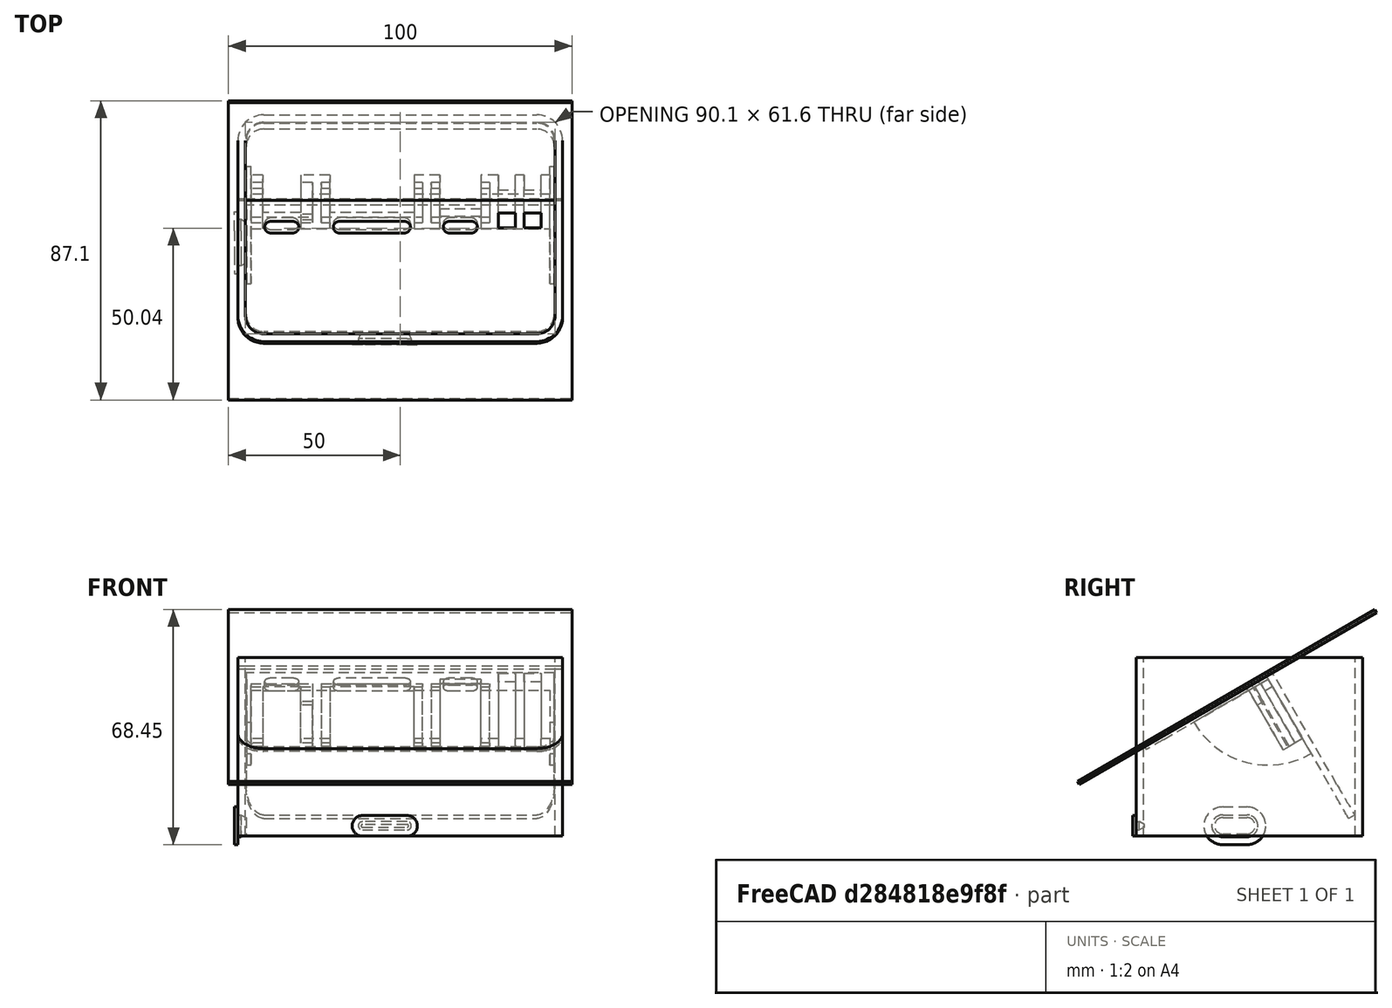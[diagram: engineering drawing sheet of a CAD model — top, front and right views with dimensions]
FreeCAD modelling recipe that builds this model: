
FCSTD DOCUMENT  (FreeCAD 0.21R33771 (Git))
Label: 2432S028_zz01
License: All rights reserved
LicenseURL: http://en.wikipedia.org/wiki/All_rights_reserved
objects: Part::Extrusion×22, Sketcher::SketchObject×21, Part::Box×9, Part::FeaturePython×8, Part::Cut×7, Part::Chamfer×6, Mesh::Feature×3, Part::MultiCommon×1, Part::MultiFuse×1
note: 75 computed .brp shape members not serialized (recipe doc carries the construction recipe); baked Part::Feature solids carry a one-line shape summary decoded from their .brp

FEATURE [Sketcher::SketchObject] Sketch  label="Basis"
  FullyConstrained = true
  sketch-geometry (22):
    g0: LineSegment StartX=-39.75 StartY=33 StartZ=0 EndX=39.75 EndY=33 EndZ=0
    g1: LineSegment StartX=47.25 StartY=25.5 StartZ=0 EndX=47.25 EndY=-25.5 EndZ=0
    g2: LineSegment StartX=39.75 StartY=-33 StartZ=0 EndX=-39.75 EndY=-33 EndZ=0
    g3: LineSegment StartX=-47.25 StartY=-25.5 StartZ=0 EndX=-47.25 EndY=25.5 EndZ=0
    g4: ArcOfCircle CenterX=-39.75 CenterY=25.5 CenterZ=0 NormalX=0 NormalY=0 NormalZ=1 AngleXU=0 Radius=7.5 StartAngle=1.5708 EndAngle=3.14159
    g5: GeomPoint X=-47.25 Y=33 Z=0
    g6: ArcOfCircle CenterX=39.75 CenterY=25.5 CenterZ=0 NormalX=0 NormalY=0 NormalZ=1 AngleXU=0 Radius=7.5 StartAngle=0 EndAngle=1.5708
    g7: GeomPoint X=47.25 Y=33 Z=0
    g8: ArcOfCircle CenterX=39.75 CenterY=-25.5 CenterZ=0 NormalX=0 NormalY=0 NormalZ=1 AngleXU=0 Radius=7.5 StartAngle=4.71239 EndAngle=6.28319
    g9: GeomPoint X=47.25 Y=-33 Z=0
    g10: ArcOfCircle CenterX=-39.75 CenterY=-25.5 CenterZ=0 NormalX=0 NormalY=0 NormalZ=1 AngleXU=0 Radius=7.5 StartAngle=3.14159 EndAngle=4.71239
    g11: GeomPoint X=-47.25 Y=-33 Z=0
    g12: ArcOfCircle CenterX=39.75 CenterY=17.9 CenterZ=0 NormalX=0 NormalY=0 NormalZ=1 AngleXU=0 Radius=5.5 StartAngle=4e-16 EndAngle=1.5708
    g13: LineSegment StartX=45.25 StartY=17.9 StartZ=0 EndX=45.25 EndY=-25.5 EndZ=0
    g14: ArcOfCircle CenterX=39.75 CenterY=-25.5 CenterZ=0 NormalX=0 NormalY=0 NormalZ=1 AngleXU=0 Radius=5.5 StartAngle=4.71239 EndAngle=6.28319
    g15: LineSegment StartX=39.75 StartY=-31 StartZ=0 EndX=-39.75 EndY=-31 EndZ=0
    g16: ArcOfCircle CenterX=-39.75 CenterY=-25.5 CenterZ=0 NormalX=0 NormalY=0 NormalZ=1 AngleXU=0 Radius=5.5 StartAngle=3.14159 EndAngle=4.71239
    g17: LineSegment StartX=-45.25 StartY=-25.5 StartZ=0 EndX=-45.25 EndY=17.9 EndZ=0
    g18: ArcOfCircle CenterX=-39.75 CenterY=17.9 CenterZ=0 NormalX=0 NormalY=0 NormalZ=1 AngleXU=0 Radius=5.5 StartAngle=1.5708 EndAngle=3.14159
    g19: LineSegment StartX=-39.75 StartY=23.4 StartZ=0 EndX=39.75 EndY=23.4 EndZ=0
    g20: GeomPoint X=45.25 Y=23.4 Z=0
    g21: GeomPoint X=-45.25 Y=-31 Z=0
  constraints (50):
    c: Horizontal(g0)
    c: Horizontal(g2)
    c: Vertical(g1)
    c: Vertical(g3)
    c: DistanceY(g9,g7) = 66
    c: Symmetric(g5,g9,g-1)
    c: PointOnObject(g5,g0)
    c: PointOnObject(g5,g3)
    c: Tangent(g0,g4) = 1.5708
    c: Tangent(g3,g4) = 1.5708
    c: PointOnObject(g7,g0)
    c: PointOnObject(g7,g1)
    c: Tangent(g0,g6) = 1.5708
    c: Tangent(g1,g6) = 1.5708
    c: PointOnObject(g9,g1)
    c: PointOnObject(g9,g2)
    c: Tangent(g1,g8) = 1.5708
    c: Tangent(g2,g8) = 1.5708
    c: PointOnObject(g11,g2)
    c: PointOnObject(g11,g3)
    c: Tangent(g2,g10) = 1.5708
    c: Tangent(g3,g10) = 1.5708
    c: Equal(g8,g10)
    c: Equal(g10,g4)
    c: Equal(g4,g6)
    c: Tangent(g12,g13) = 1.5708
    c: Tangent(g13,g14) = 1.5708
    c: Tangent(g14,g15) = 1.5708
    c: Tangent(g15,g16) = 1.5708
    c: Tangent(g16,g17) = 1.5708
    c: Tangent(g17,g18) = 1.5708
    c: Tangent(g18,g19) = 1.5708
    c: Tangent(g19,g12) = 1.5708
    c: Horizontal(g15)
    c: Vertical(g13)
    c: Vertical(g17)
    c: Equal(g12,g14)
    c: Equal(g14,g16)
    c: Equal(g16,g18)
    c: PointOnObject(g20,g13)
    c: PointOnObject(g20,g19)
    c: PointOnObject(g21,g15)
    c: PointOnObject(g21,g17)
    c: DistanceY(g14,g12) = 54.4
    c: DistanceX(g17,g12) = 90.5
    c: Diameter(g12) = 11
    c: Symmetric(g12,g17,g-2)
    c: DistanceY(g2,g14) = 2
    c: Coincident(g10,g16)
    c: DistanceY(g18,g4) = 2.1
FEATURE [Part::Box] Box  label="Cube"
  AttacherType = Attacher::AttachEngine3D
  Height = 100
  Length = 100
  Placement = pos=(-50,39.3072,-0.4) rot=(1,0,0;0.523599rad)
  Width = 100
FEATURE [Sketcher::SketchObject] Sketch001
  ExternalGeometry = -> [Sketch]
  FullyConstrained = true
  sketch-geometry (20):
    g0: ArcOfCircle CenterX=-39.75 CenterY=25.5 CenterZ=0 NormalX=0 NormalY=0 NormalZ=1 AngleXU=0 Radius=7.5 StartAngle=1.5708 EndAngle=3.14159
    g1: LineSegment StartX=-39.75 StartY=33 StartZ=0 EndX=39.75 EndY=33 EndZ=0
    g2: ArcOfCircle CenterX=39.75 CenterY=25.5 CenterZ=0 NormalX=0 NormalY=0 NormalZ=1 AngleXU=0 Radius=7.5 StartAngle=1e-16 EndAngle=1.5708
    g3: LineSegment StartX=47.25 StartY=25.5 StartZ=0 EndX=47.25 EndY=-25.5 EndZ=0
    g4: ArcOfCircle CenterX=39.75 CenterY=-25.5 CenterZ=0 NormalX=0 NormalY=0 NormalZ=1 AngleXU=0 Radius=7.5 StartAngle=4.71239 EndAngle=6.28319
    g5: LineSegment StartX=39.75 StartY=-33 StartZ=0 EndX=-39.75 EndY=-33 EndZ=0
    g6: ArcOfCircle CenterX=-39.75 CenterY=-25.5 CenterZ=0 NormalX=0 NormalY=0 NormalZ=1 AngleXU=0 Radius=7.5 StartAngle=3.14159 EndAngle=4.71239
    g7: LineSegment StartX=-47.25 StartY=-25.5 StartZ=0 EndX=-47.25 EndY=25.5 EndZ=0
    g8: GeomPoint X=-47.25 Y=33 Z=0
    g9: GeomPoint X=47.25 Y=-33 Z=0
    g10: ArcOfCircle CenterX=-39.75 CenterY=17.9 CenterZ=0 NormalX=0 NormalY=0 NormalZ=1 AngleXU=0 Radius=5.5 StartAngle=1.5708 EndAngle=3.14159
    g11: LineSegment StartX=-39.75 StartY=23.4 StartZ=0 EndX=39.75 EndY=23.4 EndZ=0
    g12: ArcOfCircle CenterX=39.75 CenterY=17.9 CenterZ=0 NormalX=0 NormalY=0 NormalZ=1 AngleXU=0 Radius=5.5 StartAngle=0 EndAngle=1.5708
    g13: LineSegment StartX=45.25 StartY=17.9 StartZ=0 EndX=45.25 EndY=-25.5 EndZ=0
    g14: ArcOfCircle CenterX=39.75 CenterY=-25.5 CenterZ=0 NormalX=0 NormalY=0 NormalZ=1 AngleXU=0 Radius=5.5 StartAngle=4.71239 EndAngle=6.28319
    g15: LineSegment StartX=39.75 StartY=-31 StartZ=0 EndX=-39.75 EndY=-31 EndZ=0
    g16: ArcOfCircle CenterX=-39.75 CenterY=-25.5 CenterZ=0 NormalX=0 NormalY=0 NormalZ=1 AngleXU=0 Radius=5.5 StartAngle=3.14159 EndAngle=4.71239
    g17: LineSegment StartX=-45.25 StartY=-25.5 StartZ=0 EndX=-45.25 EndY=17.9 EndZ=0
    g18: GeomPoint X=-45.25 Y=23.4 Z=0
    g19: GeomPoint X=45.25 Y=-31 Z=0
  constraints (44):
    c: Tangent(g0,g1) = 1.5708
    c: Tangent(g1,g2) = 1.5708
    c: Tangent(g2,g3) = 1.5708
    c: Tangent(g3,g4) = 1.5708
    c: Tangent(g4,g5) = 1.5708
    c: Tangent(g5,g6) = 1.5708
    c: Tangent(g6,g7) = 1.5708
    c: Tangent(g7,g0) = 1.5708
    c: Horizontal(g1)
    c: Horizontal(g5)
    c: Vertical(g3)
    c: Vertical(g7)
    c: Equal(g0,g2)
    c: Equal(g2,g4)
    c: Equal(g4,g6)
    c: PointOnObject(g8,g1)
    c: PointOnObject(g8,g7)
    c: PointOnObject(g9,g3)
    c: PointOnObject(g9,g5)
    c: Coincident(g-6,g4)
    c: Coincident(g0,g-3)
    c: Horizontal(g-3,g0)
    c: Tangent(g10,g11) = 1.5708
    c: Tangent(g11,g12) = 1.5708
    c: Tangent(g12,g13) = 1.5708
    c: Tangent(g13,g14) = 1.5708
    c: Tangent(g14,g15) = 1.5708
    c: Tangent(g15,g16) = 1.5708
    c: Tangent(g16,g17) = 1.5708
    c: Tangent(g17,g10) = 1.5708
    c: Horizontal(g11)
    c: Horizontal(g15)
    c: Vertical(g13)
    c: Vertical(g17)
    c: Equal(g10,g12)
    c: Equal(g12,g14)
    c: Equal(g14,g16)
    c: PointOnObject(g18,g11)
    c: PointOnObject(g18,g17)
    c: PointOnObject(g19,g13)
    c: PointOnObject(g19,g15)
    c: Coincident(g14,g4)
    c: Coincident(g10,g-5)
    c: Horizontal(g-5,g10)
FEATURE [Part::Extrusion] Extrude
  Base = -> Sketch001
  Dir = (0,0,1)
  DirMode = 2
  FaceMakerClass = Part::FaceMakerBullseye
  LengthFwd = 2
  LengthRev = 0
  Solid = true
  Symmetric = false
FEATURE [Sketcher::SketchObject] Sketch002
  ExternalGeometry = -> [Sketch]
  FullyConstrained = true
  Placement = pos=(0,0,2) rot=(0,0,1;0rad)
  sketch-geometry (26):
    g0: ArcOfCircle CenterX=-39.75 CenterY=25.5 CenterZ=0 NormalX=0 NormalY=0 NormalZ=1 AngleXU=0 Radius=7.5 StartAngle=1.5708 EndAngle=3.14159
    g1: LineSegment StartX=-39.75 StartY=33 StartZ=0 EndX=39.75 EndY=33 EndZ=0
    g2: ArcOfCircle CenterX=39.75 CenterY=25.5 CenterZ=0 NormalX=0 NormalY=0 NormalZ=1 AngleXU=0 Radius=7.5 StartAngle=4e-16 EndAngle=1.5708
    g3: LineSegment StartX=47.25 StartY=25.5 StartZ=0 EndX=47.25 EndY=-25.5 EndZ=0
    g4: ArcOfCircle CenterX=39.75 CenterY=-25.5 CenterZ=0 NormalX=0 NormalY=0 NormalZ=1 AngleXU=0 Radius=7.5 StartAngle=4.71239 EndAngle=6.28319
    g5: LineSegment StartX=39.75 StartY=-33 StartZ=0 EndX=-39.75 EndY=-33 EndZ=0
    g6: ArcOfCircle CenterX=-39.75 CenterY=-25.5 CenterZ=0 NormalX=0 NormalY=0 NormalZ=1 AngleXU=0 Radius=7.5 StartAngle=3.14159 EndAngle=4.71239
    g7: LineSegment StartX=-47.25 StartY=-25.5 StartZ=0 EndX=-47.25 EndY=25.5 EndZ=0
    g8: GeomPoint X=-47.25 Y=33 Z=0
    g9: GeomPoint X=47.25 Y=-33 Z=0
    g10: ArcOfCircle CenterX=-39.75 CenterY=17.9 CenterZ=0 NormalX=0 NormalY=0 NormalZ=1 AngleXU=0 Radius=5.5 StartAngle=1.5708 EndAngle=3.14159
    g11: LineSegment StartX=-39.75 StartY=23.4 StartZ=0 EndX=39.75 EndY=23.4 EndZ=0
    g12: ArcOfCircle CenterX=39.75 CenterY=17.9 CenterZ=0 NormalX=0 NormalY=0 NormalZ=1 AngleXU=0 Radius=5.5 StartAngle=0 EndAngle=1.5708
    g13: LineSegment StartX=45.25 StartY=17.9 StartZ=0 EndX=45.25 EndY=-25.5 EndZ=0
    g14: ArcOfCircle CenterX=39.75 CenterY=-25.5 CenterZ=0 NormalX=0 NormalY=0 NormalZ=1 AngleXU=0 Radius=5.5 StartAngle=4.71239 EndAngle=6.28319
    g15: LineSegment StartX=39.75 StartY=-31 StartZ=0 EndX=-39.75 EndY=-31 EndZ=0
    g16: ArcOfCircle CenterX=-39.75 CenterY=-25.5 CenterZ=0 NormalX=0 NormalY=0 NormalZ=1 AngleXU=0 Radius=5.5 StartAngle=3.14159 EndAngle=4.71239
    g17: LineSegment StartX=-45.25 StartY=-25.5 StartZ=0 EndX=-45.25 EndY=17.9 EndZ=0
    g18: GeomPoint X=-45.25 Y=23.4 Z=0
    g19: GeomPoint X=45.25 Y=-31 Z=0
    g20: ArcOfCircle CenterX=-39.75 CenterY=25.5 CenterZ=0 NormalX=0 NormalY=0 NormalZ=1 AngleXU=0 Radius=5.5 StartAngle=1.5708 EndAngle=3.14159
    g21: LineSegment StartX=-39.75 StartY=31 StartZ=0 EndX=39.75 EndY=31 EndZ=0
    g22: ArcOfCircle CenterX=39.75 CenterY=25.5 CenterZ=0 NormalX=0 NormalY=0 NormalZ=1 AngleXU=0 Radius=5.5 StartAngle=0 EndAngle=1.5708
    g23: LineSegment StartX=-45.25 StartY=25.4 StartZ=0 EndX=45.25 EndY=25.4 EndZ=0
    g24: LineSegment StartX=-45.25 StartY=25.5 StartZ=0 EndX=-45.25 EndY=25.4 EndZ=0
    g25: LineSegment StartX=45.25 StartY=25.5 StartZ=0 EndX=45.25 EndY=25.4 EndZ=0
  constraints (62):
    c: Tangent(g0,g1) = 1.5708
    c: Tangent(g1,g2) = 1.5708
    c: Tangent(g2,g3) = 1.5708
    c: Tangent(g3,g4) = 1.5708
    c: Tangent(g4,g5) = 1.5708
    c: Tangent(g5,g6) = 1.5708
    c: Tangent(g6,g7) = 1.5708
    c: Tangent(g7,g0) = 1.5708
    c: Horizontal(g1)
    c: Horizontal(g5)
    c: Vertical(g3)
    c: Vertical(g7)
    c: Equal(g0,g2)
    c: Equal(g2,g4)
    c: Equal(g4,g6)
    c: PointOnObject(g8,g1)
    c: PointOnObject(g8,g7)
    c: PointOnObject(g9,g3)
    c: PointOnObject(g9,g5)
    c: Coincident(g4,g-6)
    c: Coincident(g0,g-3)
    c: Horizontal(g-3,g0)
    c: Tangent(g10,g11) = 1.5708
    c: Tangent(g11,g12) = 1.5708
    c: Tangent(g12,g13) = 1.5708
    c: Tangent(g13,g14) = 1.5708
    c: Tangent(g14,g15) = 1.5708
    c: Tangent(g15,g16) = 1.5708
    c: Tangent(g16,g17) = 1.5708
    c: Tangent(g17,g10) = 1.5708
    c: Horizontal(g11)
    c: Horizontal(g15)
    c: Vertical(g13)
    c: Vertical(g17)
    c: Equal(g10,g12)
    c: Equal(g12,g14)
    c: Equal(g14,g16)
    c: PointOnObject(g18,g11)
    c: PointOnObject(g18,g17)
    c: PointOnObject(g19,g13)
    c: PointOnObject(g19,g15)
    c: Coincident(g4,g14)
    c: Coincident(g10,g-5)
    c: Horizontal(g14,g-6)
    c: Coincident(g20,g0)
    c: Vertical(g0,g20)
    c: Horizontal(g0,g20)
    c: DistanceY(g20,g0) = 2
    c: Coincident(g21,g20)
    c: Horizontal(g21)
    c: Coincident(g22,g2)
    c: Coincident(g22,g21)
    c: Equal(g22,g20)
    c: Horizontal(g2,g22)
    c: Horizontal(g23)
    c: Coincident(g24,g20)
    c: Coincident(g24,g23)
    c: Vertical(g24)
    c: Coincident(g25,g22)
    c: Coincident(g25,g23)
    c: Vertical(g25)
    c: DistanceY(g10,g23) = 2
FEATURE [Part::Extrusion] Extrude001  label="Extrude_2mm"
  Base = -> Sketch002
  Dir = (0,0,1)
  DirMode = 2
  FaceMakerClass = Part::FaceMakerBullseye
  LengthFwd = 2
  LengthRev = 0
  Solid = true
  Symmetric = false
FEATURE [Sketcher::SketchObject] Sketch003
  ExternalGeometry = -> [Sketch]
  FullyConstrained = true
  Placement = pos=(0,0,4) rot=(0,0,1;0rad)
  sketch-geometry (20):
    g0: ArcOfCircle CenterX=-39.75 CenterY=25.5 CenterZ=0 NormalX=0 NormalY=0 NormalZ=1 AngleXU=0 Radius=7.5 StartAngle=1.5708 EndAngle=3.14159
    g1: LineSegment StartX=-39.75 StartY=33 StartZ=0 EndX=39.75 EndY=33 EndZ=0
    g2: ArcOfCircle CenterX=39.75 CenterY=25.5 CenterZ=0 NormalX=0 NormalY=0 NormalZ=1 AngleXU=0 Radius=7.5 StartAngle=0 EndAngle=1.5708
    g3: LineSegment StartX=47.25 StartY=25.5 StartZ=0 EndX=47.25 EndY=-25.5 EndZ=0
    g4: ArcOfCircle CenterX=39.75 CenterY=-25.5 CenterZ=0 NormalX=0 NormalY=0 NormalZ=1 AngleXU=0 Radius=7.5 StartAngle=4.71239 EndAngle=6.28319
    g5: LineSegment StartX=39.75 StartY=-33 StartZ=0 EndX=-39.75 EndY=-33 EndZ=0
    g6: ArcOfCircle CenterX=-39.75 CenterY=-25.5 CenterZ=0 NormalX=0 NormalY=0 NormalZ=1 AngleXU=0 Radius=7.5 StartAngle=3.14159 EndAngle=4.71239
    g7: LineSegment StartX=-47.25 StartY=-25.5 StartZ=0 EndX=-47.25 EndY=25.5 EndZ=0
    g8: GeomPoint X=-47.25 Y=33 Z=0
    g9: GeomPoint X=47.25 Y=-33 Z=0
    g10: ArcOfCircle CenterX=-39.75 CenterY=25.5 CenterZ=0 NormalX=0 NormalY=0 NormalZ=1 AngleXU=0 Radius=5.5 StartAngle=1.5708 EndAngle=3.14159
    g11: LineSegment StartX=-39.75 StartY=31 StartZ=0 EndX=39.75 EndY=31 EndZ=0
    g12: ArcOfCircle CenterX=39.75 CenterY=25.5 CenterZ=0 NormalX=0 NormalY=0 NormalZ=1 AngleXU=0 Radius=5.5 StartAngle=0 EndAngle=1.5708
    g13: LineSegment StartX=45.25 StartY=25.5 StartZ=0 EndX=45.25 EndY=-25.5 EndZ=0
    g14: ArcOfCircle CenterX=39.75 CenterY=-25.5 CenterZ=0 NormalX=0 NormalY=0 NormalZ=1 AngleXU=0 Radius=5.5 StartAngle=4.71239 EndAngle=6.28319
    g15: LineSegment StartX=39.75 StartY=-31 StartZ=0 EndX=-39.75 EndY=-31 EndZ=0
    g16: ArcOfCircle CenterX=-39.75 CenterY=-25.5 CenterZ=0 NormalX=0 NormalY=0 NormalZ=1 AngleXU=0 Radius=5.5 StartAngle=3.14159 EndAngle=4.71239
    g17: LineSegment StartX=-45.25 StartY=-25.5 StartZ=0 EndX=-45.25 EndY=25.5 EndZ=0
    g18: GeomPoint X=-45.25 Y=31 Z=0
    g19: GeomPoint X=45.25 Y=-31 Z=0
  constraints (45):
    c: Tangent(g0,g1) = 1.5708
    c: Tangent(g1,g2) = 1.5708
    c: Tangent(g2,g3) = 1.5708
    c: Tangent(g3,g4) = 1.5708
    c: Tangent(g4,g5) = 1.5708
    c: Tangent(g5,g6) = 1.5708
    c: Tangent(g6,g7) = 1.5708
    c: Tangent(g7,g0) = 1.5708
    c: Horizontal(g1)
    c: Horizontal(g5)
    c: Vertical(g3)
    c: Vertical(g7)
    c: Equal(g0,g2)
    c: Equal(g2,g4)
    c: Equal(g4,g6)
    c: PointOnObject(g8,g1)
    c: PointOnObject(g8,g7)
    c: PointOnObject(g9,g3)
    c: PointOnObject(g9,g5)
    c: Coincident(g-5,g4)
    c: Coincident(g0,g-3)
    c: Horizontal(g-3,g0)
    c: Tangent(g10,g11) = 1.5708
    c: Tangent(g12,g13) = 1.5708
    c: Tangent(g13,g14) = 1.5708
    c: Tangent(g14,g15) = 1.5708
    c: Tangent(g15,g16) = 1.5708
    c: Tangent(g16,g17) = 1.5708
    c: Tangent(g17,g10) = 1.5708
    c: Horizontal(g11)
    c: Horizontal(g15)
    c: Vertical(g13)
    c: Vertical(g17)
    c: Equal(g10,g12)
    c: Equal(g12,g14)
    c: Equal(g14,g16)
    c: PointOnObject(g18,g11)
    c: PointOnObject(g18,g17)
    c: PointOnObject(g19,g13)
    c: PointOnObject(g19,g15)
    c: Coincident(g14,g4)
    c: Coincident(g11,g12)
    c: Coincident(g0,g10)
    c: Horizontal(g15,g-6)
    c: Vertical(g12,g11)
FEATURE [Part::Extrusion] Extrude002  label="Extrude_4mm"
  Base = -> Sketch003
  Dir = (0,0,1)
  DirMode = 2
  FaceMakerClass = Part::FaceMakerBullseye
  LengthFwd = 10
  LengthRev = 0
  Solid = true
  Symmetric = false
FEATURE [Part::Extrusion] Extrude003  label="Extrude_6mm"
  Base = -> Sketch003
  Dir = (0,0,1)
  DirMode = 2
  FaceMakerClass = Part::FaceMakerBullseye
  LengthFwd = 52
  LengthRev = 0
  Solid = true
  Symmetric = false
FEATURE [Part::Box] Box001  label="Cube001"
  AttacherType = Attacher::AttachEngine3D
  Height = 100
  Length = 100
  Placement = pos=(-50,-49.5397,19.0874) rot=(1,0,0;0.523599rad)
  Width = 100
FEATURE [Part::Box] Box002  label="Cube002"
  AttacherType = Attacher::AttachEngine3D
  Height = 100
  Length = 100
  Placement = pos=(-50,37.5751,-1.4) rot=(1,0,0;0.523599rad)
  Width = 2
FEATURE [Sketcher::SketchObject] Sketch004
  ExternalGeometry = -> [Sketch]
  FullyConstrained = false
  sketch-geometry (12):
    g0: ArcOfCircle CenterX=-39.75 CenterY=25.5 CenterZ=0 NormalX=0 NormalY=0 NormalZ=1 AngleXU=0 Radius=7.5 StartAngle=1.5708 EndAngle=3.14159
    g1: LineSegment StartX=-39.75 StartY=33 StartZ=0 EndX=39.75 EndY=33 EndZ=0
    g2: ArcOfCircle CenterX=39.75 CenterY=25.5 CenterZ=0 NormalX=0 NormalY=0 NormalZ=1 AngleXU=0 Radius=7.5 StartAngle=1e-16 EndAngle=1.5708
    g3: LineSegment StartX=47.25 StartY=25.5 StartZ=0 EndX=47.25 EndY=-25.5 EndZ=0
    g4: ArcOfCircle CenterX=39.75 CenterY=-25.5 CenterZ=0 NormalX=0 NormalY=0 NormalZ=1 AngleXU=0 Radius=7.5 StartAngle=4.71239 EndAngle=6.28319
    g5: LineSegment StartX=39.75 StartY=-33 StartZ=0 EndX=-39.75 EndY=-33 EndZ=0
    g6: ArcOfCircle CenterX=-39.75 CenterY=-25.5 CenterZ=0 NormalX=0 NormalY=0 NormalZ=1 AngleXU=0 Radius=7.5 StartAngle=3.14159 EndAngle=4.71239
    g7: LineSegment StartX=-47.25 StartY=-25.5 StartZ=0 EndX=-47.25 EndY=25.5 EndZ=0
    g8: GeomPoint X=-47.25 Y=33 Z=0
    g9: GeomPoint X=47.25 Y=-33 Z=0
    g10: GeomPoint X=-22 Y=14 Z=0
    g11: GeomPoint X=22 Y=-30 Z=0
  constraints (22):
    c: Tangent(g0,g1) = 1.5708
    c: Tangent(g1,g2) = 1.5708
    c: Tangent(g2,g3) = 1.5708
    c: Tangent(g3,g4) = 1.5708
    c: Tangent(g4,g5) = 1.5708
    c: Tangent(g5,g6) = 1.5708
    c: Tangent(g6,g7) = 1.5708
    c: Tangent(g7,g0) = 1.5708
    c: Horizontal(g1)
    c: Horizontal(g5)
    c: Vertical(g3)
    c: Vertical(g7)
    c: Equal(g0,g2)
    c: Equal(g2,g4)
    c: Equal(g4,g6)
    c: PointOnObject(g8,g1)
    c: PointOnObject(g8,g7)
    c: PointOnObject(g9,g3)
    c: PointOnObject(g9,g5)
    c: Coincident(g0,g-3)
    c: Horizontal(g-3,g0)
    c: Coincident(g4,g-4)
FEATURE [Part::Extrusion] Extrude004
  Base = -> Sketch004
  Dir = (0,0,1)
  DirMode = 2
  FaceMakerClass = Part::FaceMakerBullseye
  LengthFwd = 56
  LengthRev = 0
  Solid = true
  Symmetric = false
FEATURE [Part::MultiCommon] Common
  Shapes = -> [Box002,Extrude004]
FEATURE [Part::MultiFuse] Fusion
  Shapes = -> [Common,Extrude,Extrude001,Extrude002,Extrude003]
FEATURE [Part::Cut] Cut
  Base = -> Fusion
  Tool = -> Box
FEATURE [Part::Cut] Cut001
  Base = -> Cut
  Tool = -> Box001
FEATURE [Part::Box] Box003  label="Cube003"
  AttacherType = Attacher::AttachEngine3D
  Height = 3
  Length = 1.5
  Placement = pos=(43.75,-29,7) rot=(0,0,1;0rad)
  Width = 14.7
FEATURE [Part::Chamfer] Chamfer
  Base = -> Box003
  Edges = 4 edges r=1.49: [Edge1,Edge2,Edge3,Edge4]
FEATURE [Part::Box] Box004  label="Cube004"
  AttacherType = Attacher::AttachEngine3D
  Height = 3
  Length = 1.5
  Placement = pos=(-45.25,-29,8) rot=(0,0,1;0rad)
  Width = 14.7
FEATURE [Part::Chamfer] Chamfer001
  Base = -> Box004
  Edges = 4 edges r=1.49: [Edge5,Edge6,Edge7,Edge8]
FEATURE [Sketcher::SketchObject] Sketch005  label="Basis001_bEZEL"
  FullyConstrained = true
  Placement = pos=(0,-2.75,0) rot=(0,1,0;3.14159rad)
  sketch-geometry (46):
    g0: ArcOfCircle CenterX=40 CenterY=22 CenterZ=0 NormalX=0 NormalY=0 NormalZ=1 AngleXU=0 Radius=3 StartAngle=4e-16 EndAngle=1.5708
    g1: LineSegment StartX=43 StartY=22 StartZ=0 EndX=43 EndY=-22 EndZ=0
    g2: ArcOfCircle CenterX=40 CenterY=-22 CenterZ=0 NormalX=0 NormalY=0 NormalZ=1 AngleXU=0 Radius=3 StartAngle=4.71239 EndAngle=6.28319
    g3: LineSegment StartX=40 StartY=-25 StartZ=0 EndX=-40 EndY=-25 EndZ=0
    g4: ArcOfCircle CenterX=-40 CenterY=-22 CenterZ=0 NormalX=0 NormalY=0 NormalZ=1 AngleXU=0 Radius=3 StartAngle=3.14159 EndAngle=4.71239
    g5: LineSegment StartX=-43 StartY=-22 StartZ=0 EndX=-43 EndY=22 EndZ=0
    g6: ArcOfCircle CenterX=-40 CenterY=22 CenterZ=0 NormalX=0 NormalY=0 NormalZ=1 AngleXU=0 Radius=3 StartAngle=1.5708 EndAngle=3.14159
    g7: LineSegment StartX=-40 StartY=25 StartZ=0 EndX=40 EndY=25 EndZ=0
    g8: GeomPoint X=43 Y=25 Z=0
    g9: GeomPoint X=-43 Y=-25 Z=0
    g10: Circle CenterX=-39 CenterY=21 CenterZ=0 NormalX=0 NormalY=0 NormalZ=1 AngleXU=0 Radius=1.6
    g11: Circle CenterX=-39 CenterY=-21 CenterZ=0 NormalX=0 NormalY=0 NormalZ=1 AngleXU=0 Radius=1.6
    g12: Circle CenterX=39 CenterY=21 CenterZ=0 NormalX=0 NormalY=0 NormalZ=1 AngleXU=0 Radius=1.6
    g13: Circle CenterX=39 CenterY=-21 CenterZ=0 NormalX=0 NormalY=0 NormalZ=1 AngleXU=0 Radius=1.6
    g14: LineSegment StartX=-35 StartY=25 StartZ=0 EndX=36 EndY=25 EndZ=0
    g15: LineSegment StartX=36 StartY=25 StartZ=0 EndX=36 EndY=-25 EndZ=0
    g16: LineSegment StartX=36 StartY=-25 StartZ=0 EndX=-35 EndY=-25 EndZ=0
    g17: LineSegment StartX=-35 StartY=-25 StartZ=0 EndX=-35 EndY=25 EndZ=0
    g18: LineSegment StartX=-40.4 StartY=-12 StartZ=0 EndX=-37.4 EndY=-12 EndZ=0
    g19: LineSegment StartX=-37.4 StartY=-12 StartZ=0 EndX=-37.4 EndY=-17 EndZ=0
    g20: LineSegment StartX=-37.4 StartY=-17 StartZ=0 EndX=-40.4 EndY=-17 EndZ=0
    g21: LineSegment StartX=-40.4 StartY=-17 StartZ=0 EndX=-40.4 EndY=-12 EndZ=0
    g22: LineSegment StartX=-2 StartY=-25 StartZ=0 EndX=11 EndY=-25 EndZ=0
    g23: LineSegment StartX=11 StartY=-25 StartZ=0 EndX=11 EndY=-28 EndZ=0
    g24: LineSegment StartX=11 StartY=-28 StartZ=0 EndX=-2 EndY=-28 EndZ=0
    g25: LineSegment StartX=-2 StartY=-28 StartZ=0 EndX=-2 EndY=-25 EndZ=0
    g26: LineSegment StartX=43 StartY=3 StartZ=0 EndX=53 EndY=3 EndZ=0
    g27: LineSegment StartX=53 StartY=3 StartZ=0 EndX=53 EndY=-6 EndZ=0
    g28: LineSegment StartX=53 StartY=-6 StartZ=0 EndX=43 EndY=-6 EndZ=0
    g29: LineSegment StartX=43 StartY=-6 StartZ=0 EndX=43 EndY=3 EndZ=0
    g30: LineSegment StartX=43 StartY=14 StartZ=0 EndX=45 EndY=14 EndZ=0
    g31: LineSegment StartX=45 StartY=14 StartZ=0 EndX=45 EndY=6 EndZ=0
    g32: LineSegment StartX=45 StartY=6 StartZ=0 EndX=43 EndY=6 EndZ=0
    g33: LineSegment StartX=43 StartY=6 StartZ=0 EndX=43 EndY=14 EndZ=0
    g34: LineSegment StartX=-31.5 StartY=-25 StartZ=0 EndX=-23.5 EndY=-25 EndZ=0
    g35: LineSegment StartX=-23.5 StartY=-25 StartZ=0 EndX=-23.5 EndY=-27 EndZ=0
    g36: LineSegment StartX=-23.5 StartY=-27 StartZ=0 EndX=-31.5 EndY=-27 EndZ=0
    g37: LineSegment StartX=-31.5 StartY=-27 StartZ=0 EndX=-31.5 EndY=-25 EndZ=0
    g38: LineSegment StartX=-16.5 StartY=-25 StartZ=0 EndX=-8.5 EndY=-25 EndZ=0
    g39: LineSegment StartX=-8.5 StartY=-25 StartZ=0 EndX=-8.5 EndY=-27 EndZ=0
    g40: LineSegment StartX=-8.5 StartY=-27 StartZ=0 EndX=-16.5 EndY=-27 EndZ=0
    g41: LineSegment StartX=-16.5 StartY=-27 StartZ=0 EndX=-16.5 EndY=-25 EndZ=0
    g42: LineSegment StartX=-33 StartY=22.5 StartZ=0 EndX=27 EndY=22.5 EndZ=0
    g43: LineSegment StartX=27 StartY=22.5 StartZ=0 EndX=27 EndY=-22.5 EndZ=0
    g44: LineSegment StartX=27 StartY=-22.5 StartZ=0 EndX=-33 EndY=-22.5 EndZ=0
    g45: LineSegment StartX=-33 StartY=-22.5 StartZ=0 EndX=-33 EndY=22.5 EndZ=0
  constraints (130):
    c: Tangent(g0,g1) = 1.5708
    c: Tangent(g1,g2) = 1.5708
    c: Tangent(g2,g3) = 1.5708
    c: Tangent(g3,g4) = 1.5708
    c: Tangent(g4,g5) = 1.5708
    c: Tangent(g5,g6) = 1.5708
    c: Tangent(g6,g7) = 1.5708
    c: Tangent(g7,g0) = 1.5708
    c: Horizontal(g3)
    c: Vertical(g1)
    c: Vertical(g5)
    c: Equal(g0,g2)
    c: Equal(g2,g4)
    c: Equal(g4,g6)
    c: PointOnObject(g8,g1)
    c: PointOnObject(g8,g7)
    c: PointOnObject(g9,g3)
    c: PointOnObject(g9,g5)
    c: DistanceY(g2,g0) = 50
    c: DistanceX(g5,g0) = 86
    c: Diameter(g0) = 6
    c: Symmetric(g6,g2,g-1)
    c: Horizontal(g7)
    c: Diameter(g10) = 3.2
    c: DistanceY(g10,g6) = 4
    c: DistanceX(g5,g10) = 4
    c: Equal(g10,g12)
    c: Horizontal(g10,g12)
    c: Vertical(g10,g11)
    c: Horizontal(g11,g13)
    c: Vertical(g13,g12)
    c: Equal(g10,g11)
    c: Equal(g11,g13)
    c: DistanceY(g2,g13) = 4
    c: DistanceX(g13,g1) = 4
    c: Coincident(g14,g15)
    c: Coincident(g15,g16)
    c: Coincident(g16,g17)
    c: Coincident(g17,g14)
    c: Horizontal(g14)
    c: Horizontal(g16)
    c: Vertical(g15)
    c: Vertical(g17)
    c: PointOnObject(g14,g7)
    c: PointOnObject(g16,g3)
    c: DistanceX(g14,g0) = 7
    c: DistanceX(g5,g14) = 8
    c: Coincident(g18,g19)
    c: Coincident(g19,g20)
    c: Coincident(g20,g21)
    c: Coincident(g21,g18)
    c: Horizontal(g18)
    c: Horizontal(g20)
    c: Vertical(g19)
    c: Vertical(g21)
    c: DistanceX(g20,g20) = 3
    c: DistanceY(g21,g21) = 5
    c: DistanceY(g3,g20) = 8
    c: DistanceX(g4,g20) = 2.6
    c: Coincident(g22,g23)
    c: Coincident(g23,g24)
    c: Coincident(g24,g25)
    c: Coincident(g25,g22)
    c: Horizontal(g22)
    c: Horizontal(g24)
    c: Vertical(g23)
    c: Vertical(g25)
    c: PointOnObject(g22,g3)
    c: DistanceX(g4,g22) = 41
    c: DistanceX(g22,g1) = 32
    c: DistanceY(g23,g23) = 3
    c: Coincident(g26,g27)
    c: Coincident(g27,g28)
    c: Coincident(g28,g29)
    c: Coincident(g29,g26)
    c: Horizontal(g26)
    c: Horizontal(g28)
    c: Vertical(g27)
    c: Vertical(g29)
    c: PointOnObject(g26,g1)
    c: DistanceY(g26,g0) = 22
    c: DistanceY(g2,g28) = 19
    c: DistanceX(g26,g26) = 10
    c: Coincident(g30,g31)
    c: Coincident(g31,g32)
    c: Coincident(g32,g33)
    c: Coincident(g33,g30)
    c: Horizontal(g30)
    c: Horizontal(g32)
    c: Vertical(g31)
    c: Vertical(g33)
    c: PointOnObject(g30,g1)
    c: DistanceY(g30,g0) = 11
    c: DistanceY(g2,g32) = 31
    c: DistanceX(g30,g30) = 2
    c: Coincident(g34,g35)
    c: Coincident(g35,g36)
    c: Coincident(g36,g37)
    c: Coincident(g37,g34)
    c: Horizontal(g34)
    c: Horizontal(g36)
    c: Vertical(g35)
    c: Vertical(g37)
    c: PointOnObject(g34,g3)
    c: Coincident(g38,g39)
    c: Coincident(g39,g40)
    c: Coincident(g40,g41)
    c: Coincident(g41,g38)
    c: Horizontal(g38)
    c: Horizontal(g40)
    c: Vertical(g39)
    c: Vertical(g41)
    c: PointOnObject(g38,g3)
    c: Equal(g31,g40)
    c: Equal(g40,g36)
    c: Equal(g32,g39)
    c: Equal(g39,g35)
    c: DistanceX(g4,g34) = 11.5
    c: DistanceX(g4,g38) = 26.5
    c: Coincident(g42,g43)
    c: Coincident(g43,g44)
    c: Coincident(g44,g45)
    c: Coincident(g45,g42)
    c: Horizontal(g42)
    c: Horizontal(g44)
    c: Vertical(g43)
    c: DistanceX(g44,g44) = 60
    c: DistanceY(g43,g43) = 45
    c: Symmetric(g42,g44,g-1)
    c: DistanceX(g14,g42) = 2
FEATURE [Sketcher::SketchObject] Sketch006
  ExternalGeometry = -> [Sketch005]
  FullyConstrained = true
  MapMode = 5
  Placement = pos=(0,-33,0) rot=(1,0,0;1.5708rad)
  Support = -> [Cut001]
  sketch-geometry (4):
    g0: ArcOfCircle CenterX=2 CenterY=7 CenterZ=0 NormalX=0 NormalY=0 NormalZ=1 AngleXU=0 Radius=1.5 StartAngle=4.71239 EndAngle=7.85398
    g1: ArcOfCircle CenterX=-11 CenterY=7 CenterZ=0 NormalX=0 NormalY=0 NormalZ=1 AngleXU=0 Radius=1.5 StartAngle=1.5708 EndAngle=4.71239
    g2: LineSegment StartX=2 StartY=8.5 StartZ=0 EndX=-11 EndY=8.5 EndZ=0
    g3: LineSegment StartX=-11 StartY=5.5 StartZ=0 EndX=2 EndY=5.5 EndZ=0
  constraints (10):
    c: Tangent(g0,g2) = -1.5708
    c: Tangent(g2,g1) = -1.5708
    c: Tangent(g1,g3) = -1.5708
    c: Tangent(g3,g0) = -1.5708
    c: Equal(g0,g1)
    c: Horizontal(g2)
    c: DistanceY(g-1,g1) = 7
    c: Diameter(g1) = 3
    c: Vertical(g1,g-3)
    c: Vertical(g0,g-3)
FEATURE [Part::Extrusion] Extrude005
  Base = -> Sketch006
  Dir = (0,-1,2e-16)
  DirMode = 2
  FaceMakerClass = Part::FaceMakerBullseye
  LengthFwd = 3
  LengthRev = 0
  Reversed = true
  Solid = true
  Symmetric = false
FEATURE [Sketcher::SketchObject] Sketch007
  ExternalGeometry = -> [Sketch005]
  FullyConstrained = true
  MapMode = 5
  Placement = pos=(-47.25,0,0) rot=(0.57735,-0.57735,-0.57735;2.0944rad)
  Support = -> [Cut001]
  sketch-geometry (6):
    g0: ArcOfCircle CenterX=0.75 CenterY=7 CenterZ=0 NormalX=0 NormalY=0 NormalZ=1 AngleXU=0 Radius=3.5 StartAngle=1.5708 EndAngle=4.71239
    g1: ArcOfCircle CenterX=7.75 CenterY=7 CenterZ=0 NormalX=0 NormalY=0 NormalZ=1 AngleXU=0 Radius=3.5 StartAngle=4.71239 EndAngle=7.85398
    g2: LineSegment StartX=0.75 StartY=3.5 StartZ=0 EndX=7.75 EndY=3.5 EndZ=0
    g3: LineSegment StartX=7.75 StartY=10.5 StartZ=0 EndX=0.75 EndY=10.5 EndZ=0
    g4: LineSegment StartX=-0.25 StartY=-6.5e-15 StartZ=0 EndX=0.75 EndY=3.5 EndZ=0
    g5: LineSegment StartX=7.75 StartY=3.5 StartZ=0 EndX=8.75 EndY=-6.7e-15 EndZ=0
  constraints (14):
    c: Tangent(g0,g2) = -1.5708
    c: Tangent(g2,g1) = -1.5708
    c: Tangent(g1,g3) = -1.5708
    c: Tangent(g3,g0) = -1.5708
    c: Equal(g0,g1)
    c: Horizontal(g2)
    c: DistanceY(g-1,g1) = 7
    c: Diameter(g1) = 7
    c: DistanceX(g3,g3) = 7
    c: Coincident(g4,g-3)
    c: Coincident(g4,g0)
    c: Coincident(g5,g1)
    c: Coincident(g5,g-3)
    c: Equal(g5,g4)
FEATURE [Part::Extrusion] Extrude006
  Base = -> Sketch007
  Dir = (-1,0,0)
  DirMode = 2
  FaceMakerClass = Part::FaceMakerBullseye
  LengthFwd = 3
  LengthRev = 0
  Reversed = true
  Solid = true
  Symmetric = false
FEATURE [Part::Box] Box005  label="Cube005"
  AttacherType = Attacher::AttachEngine3D
  Height = 3
  Length = 1.5
  Placement = pos=(43.75,10,7) rot=(0,0,1;0rad)
  Width = 14.7
FEATURE [Part::Chamfer] Chamfer002
  Base = -> Box005
  Edges = 4 edges r=1.49: [Edge1,Edge2,Edge3,Edge4]
FEATURE [Part::Box] Box006  label="Cube006"
  AttacherType = Attacher::AttachEngine3D
  Height = 3
  Length = 1.5
  Placement = pos=(-45.25,10,8) rot=(0,0,1;0rad)
  Width = 14.7
FEATURE [Part::Chamfer] Chamfer003
  Base = -> Box006
  Edges = 4 edges r=1.49: [Edge5,Edge6,Edge7,Edge8]
FEATURE [Part::Cut] Cut002
  Base = -> Cut001
  Tool = -> Extrude005
FEATURE [Part::Cut] Cut003
  Base = -> Cut002
  Tool = -> Extrude006
FEATURE [Part::FeaturePython] Connect  label="Main"  # WARN: FeaturePython — macro-defined, semantics opaque (R4)
  Objects = -> [Chamfer,Chamfer001,Chamfer002,Chamfer003,Cut003]
  Tolerance = 0
FEATURE [Mesh::Feature] Mesh  label="Main (Meshed)"
FEATURE [Sketcher::SketchObject] Sketch008
  ExternalGeometry = -> [Sketch007]
  FullyConstrained = true
  MapMode = 2
  Placement = pos=(-47.25,0,0) rot=(0.57735,-0.57735,-0.57735;2.0944rad)
  Support = -> [Sketch007]
  sketch-geometry (4):
    g0: ArcOfCircle CenterX=0.75 CenterY=7 CenterZ=0 NormalX=0 NormalY=0 NormalZ=1 AngleXU=0 Radius=3.2 StartAngle=1.5708 EndAngle=4.71239
    g1: ArcOfCircle CenterX=7.75 CenterY=7 CenterZ=0 NormalX=0 NormalY=0 NormalZ=1 AngleXU=0 Radius=3.2 StartAngle=4.71239 EndAngle=7.85398
    g2: LineSegment StartX=0.75 StartY=3.8 StartZ=0 EndX=7.75 EndY=3.8 EndZ=0
    g3: LineSegment StartX=7.75 StartY=10.2 StartZ=0 EndX=0.75 EndY=10.2 EndZ=0
  constraints (9):
    c: Radius(g-3) = 3.5
    c: Tangent(g0,g2) = -1.5708
    c: Tangent(g2,g1) = -1.5708
    c: Tangent(g1,g3) = -1.5708
    c: Tangent(g3,g0) = -1.5708
    c: Equal(g0,g1)
    c: Coincident(g0,g-3)
    c: Coincident(g1,g-4)
    c: Radius(g0) = 3.2
FEATURE [Part::Extrusion] Extrude007
  Base = -> Sketch008
  Dir = (-1,0,0)
  DirMode = 2
  FaceMakerClass = Part::FaceMakerBullseye
  LengthFwd = 2.4
  LengthRev = 0
  Reversed = true
  Solid = true
  Symmetric = false
FEATURE [Part::Chamfer] Chamfer004
  Base = -> Extrude007
  Edges = 1 edges: [Edge7 r1=1.5 r2=0.8]
FEATURE [Sketcher::SketchObject] Sketch009
  ExternalGeometry = -> [Sketch007]
  FullyConstrained = true
  MapMode = 2
  Placement = pos=(-47.25,0,0) rot=(0.57735,-0.57735,-0.57735;2.0944rad)
  Support = -> [Sketch007]
  sketch-geometry (4):
    g0: ArcOfCircle CenterX=0.75 CenterY=7 CenterZ=0 NormalX=0 NormalY=0 NormalZ=1 AngleXU=0 Radius=5.5 StartAngle=1.5708 EndAngle=4.71239
    g1: ArcOfCircle CenterX=7.75 CenterY=7 CenterZ=0 NormalX=0 NormalY=0 NormalZ=1 AngleXU=0 Radius=5.5 StartAngle=4.71239 EndAngle=7.85398
    g2: LineSegment StartX=0.75 StartY=1.5 StartZ=0 EndX=7.75 EndY=1.5 EndZ=0
    g3: LineSegment StartX=7.75 StartY=12.5 StartZ=0 EndX=0.75 EndY=12.5 EndZ=0
  constraints (9):
    c: Radius(g-3) = 3.5
    c: Tangent(g0,g2) = -1.5708
    c: Tangent(g2,g1) = -1.5708
    c: Tangent(g1,g3) = -1.5708
    c: Tangent(g3,g0) = -1.5708
    c: Equal(g0,g1)
    c: Coincident(g0,g-3)
    c: Coincident(g1,g-4)
    c: Radius(g0) = 5.5
FEATURE [Part::Extrusion] Extrude008
  Base = -> Sketch009
  Dir = (-1,0,0)
  DirMode = 2
  FaceMakerClass = Part::FaceMakerBullseye
  LengthFwd = 1
  LengthRev = 0
  Solid = true
  Symmetric = false
FEATURE [Part::FeaturePython] Connect001  label="Deckel_USB"  # WARN: FeaturePython — macro-defined, semantics opaque (R4)
  Objects = -> [Chamfer004,Extrude008]
  Tolerance = 0
FEATURE [Mesh::Feature] Mesh001  label="Deckel_USB (Meshed)"
  Placement = pos=(-57.5,0,48.25) rot=(0,1,0;4.71239rad)
FEATURE [Sketcher::SketchObject] Sketch010
  ExternalGeometry = -> [Sketch006]
  FullyConstrained = true
  MapMode = 2
  Placement = pos=(0,-33,0) rot=(1,0,0;1.5708rad)
  Support = -> [Sketch006]
  sketch-geometry (4):
    g0: ArcOfCircle CenterX=-11 CenterY=7 CenterZ=0 NormalX=0 NormalY=0 NormalZ=1 AngleXU=0 Radius=1.2 StartAngle=1.5708 EndAngle=4.71239
    g1: ArcOfCircle CenterX=2 CenterY=7 CenterZ=0 NormalX=0 NormalY=0 NormalZ=1 AngleXU=0 Radius=1.2 StartAngle=4.71239 EndAngle=7.85398
    g2: LineSegment StartX=-11 StartY=5.8 StartZ=0 EndX=2 EndY=5.8 EndZ=0
    g3: LineSegment StartX=2 StartY=8.2 StartZ=0 EndX=-11 EndY=8.2 EndZ=0
  constraints (9):
    c: Tangent(g0,g2) = -1.5708
    c: Tangent(g2,g1) = -1.5708
    c: Tangent(g1,g3) = -1.5708
    c: Tangent(g3,g0) = -1.5708
    c: Equal(g0,g1)
    c: Coincident(g0,g-3)
    c: Coincident(g1,g-4)
    c: Radius(g-3) = 1.5
    c: Radius(g0) = 1.2
FEATURE [Part::Extrusion] Extrude009
  Base = -> Sketch010
  Dir = (0,-1,2e-16)
  DirMode = 2
  FaceMakerClass = Part::FaceMakerBullseye
  LengthFwd = 2.4
  LengthRev = 0
  Reversed = true
  Solid = true
  Symmetric = false
FEATURE [Sketcher::SketchObject] Sketch011
  ExternalGeometry = -> [Sketch006]
  FullyConstrained = true
  MapMode = 2
  Placement = pos=(0,-33,0) rot=(1,0,0;1.5708rad)
  Support = -> [Sketch006]
  sketch-geometry (4):
    g0: ArcOfCircle CenterX=-11 CenterY=7 CenterZ=0 NormalX=0 NormalY=0 NormalZ=1 AngleXU=0 Radius=3 StartAngle=1.5708 EndAngle=4.71239
    g1: ArcOfCircle CenterX=2 CenterY=7 CenterZ=0 NormalX=0 NormalY=0 NormalZ=1 AngleXU=0 Radius=3 StartAngle=4.71239 EndAngle=7.85398
    g2: LineSegment StartX=-11 StartY=4 StartZ=0 EndX=2 EndY=4 EndZ=0
    g3: LineSegment StartX=2 StartY=10 StartZ=0 EndX=-11 EndY=10 EndZ=0
  constraints (9):
    c: Tangent(g0,g2) = -1.5708
    c: Tangent(g2,g1) = -1.5708
    c: Tangent(g1,g3) = -1.5708
    c: Tangent(g3,g0) = -1.5708
    c: Equal(g0,g1)
    c: Coincident(g0,g-3)
    c: Coincident(g1,g-4)
    c: Radius(g-3) = 1.5
    c: Radius(g0) = 3
FEATURE [Part::Extrusion] Extrude010
  Base = -> Sketch011
  Dir = (0,-1,2e-16)
  DirMode = 2
  FaceMakerClass = Part::FaceMakerBullseye
  LengthFwd = 1
  LengthRev = 0
  Solid = true
  Symmetric = false
FEATURE [Part::FeaturePython] Connect002  label="Deckel MicroSD"  # WARN: FeaturePython — macro-defined, semantics opaque (R4)
  Objects = -> [Extrude009,Extrude010]
  Tolerance = 0
FEATURE [Part::Chamfer] Chamfer005  label="Deckel MicroSD001"
  Base = -> Connect002
  Edges = 1 edges: [Edge11 r1=0.8 r2=1.5]
FEATURE [Mesh::Feature] Mesh003  label="Deckel MicroSD (Meshed)"
  Placement = pos=(0,-35.5,34) rot=(1,0,0;1.5708rad)
FEATURE [Part::Box] Box007  label="Cube007"
  AttacherType = Attacher::AttachEngine3D
  Height = 1
  Length = 100
  Placement = pos=(-50,-49.5397,19.0874) rot=(1,0,0;0.523599rad)
  Width = 100
FEATURE [Sketcher::SketchObject] Sketch012
  FullyConstrained = false
  Placement = pos=(0,-20.65,35.7668) rot=(1,0,0;3.66519rad)
  sketch-geometry (20):
    g0: LineSegment StartX=-47.25 StartY=5.6003 StartZ=0 EndX=-47.25 EndY=-31.841 EndZ=0
    g1: LineSegment StartX=-47.25 StartY=-31.841 StartZ=0 EndX=-47.25 EndY=-33.841 EndZ=0
    g2: LineSegment StartX=-47.25 StartY=-33.841 StartZ=0 EndX=-45.25 EndY=-33.841 EndZ=0
    g3: LineSegment StartX=-45.25 StartY=-33.841 StartZ=0 EndX=45.25 EndY=-33.841 EndZ=0
    g4: LineSegment StartX=45.25 StartY=-33.841 StartZ=0 EndX=47.25 EndY=-33.841 EndZ=0
    g5: LineSegment StartX=47.25 StartY=-33.841 StartZ=0 EndX=47.25 EndY=-31.841 EndZ=0
    g6: LineSegment StartX=47.25 StartY=-31.841 StartZ=0 EndX=47.25 EndY=5.6003 EndZ=0
    g7: ArcOfEllipse CenterX=39.75 CenterY=5.6003 CenterZ=0 NormalX=0 NormalY=-1e-16 NormalZ=1 MajorRadius=8.66025 MinorRadius=7.5 AngleXU=0 StartAngle=4.71239 EndAngle=6.28319
    g8: LineSegment StartX=39.75 StartY=14.2606 StartZ=0 EndX=-39.75 EndY=14.2606 EndZ=0
    g9: ArcOfEllipse CenterX=-39.75 CenterY=5.6003 CenterZ=0 NormalX=0 NormalY=-1e-16 NormalZ=1 MajorRadius=8.66025 MinorRadius=7.5 AngleXU=0 StartAngle=0 EndAngle=1.5708
    g10: ArcOfEllipse CenterX=-39.7356 CenterY=5.58989 CenterZ=0 NormalX=0 NormalY=-1e-16 NormalZ=1 MajorRadius=6.36708 MinorRadius=5.51431 AngleXU=0.0120287 StartAngle=6.27107 EndAngle=7.8407
    g11: LineSegment StartX=39.75 StartY=11.9568 StartZ=0 EndX=-39.7453 EndY=11.9568 EndZ=0
    g12: ArcOfEllipse CenterX=39.7498 CenterY=5.60031 CenterZ=0 NormalX=0 NormalY=-1e-16 NormalZ=1 MajorRadius=6.35653 MinorRadius=5.50656 AngleXU=-7.28146e-05 StartAngle=4.71245 EndAngle=6.28323
    g13: LineSegment StartX=45.2563 StartY=-31.84 StartZ=0 EndX=45.2563 EndY=5.6003 EndZ=0
    g14: LineSegment StartX=-45.25 StartY=-31.84 StartZ=0 EndX=45.2563 EndY=-31.84 EndZ=0
    g15: LineSegment StartX=-45.25 StartY=5.60814 StartZ=0 EndX=-45.25 EndY=-31.84 EndZ=0
    g16: ArcOfCircle CenterX=-26.25 CenterY=-24.34 CenterZ=0 NormalX=0 NormalY=0 NormalZ=1 AngleXU=0 Radius=4 StartAngle=4.71239 EndAngle=7.85398
    g17: ArcOfCircle CenterX=-33.25 CenterY=-24.34 CenterZ=0 NormalX=0 NormalY=0 NormalZ=1 AngleXU=0 Radius=4 StartAngle=1.5708 EndAngle=4.71239
    g18: LineSegment StartX=-26.25 StartY=-20.34 StartZ=0 EndX=-33.25 EndY=-20.34 EndZ=0
    g19: LineSegment StartX=-33.25 StartY=-28.34 StartZ=0 EndX=-26.25 EndY=-28.34 EndZ=0
  constraints (40):
    c: Vertical(g0)
    c: Coincident(g0,g1)
    c: Vertical(g1)
    c: Coincident(g1,g2)
    c: Horizontal(g2)
    c: Coincident(g2,g3)
    c: Horizontal(g3)
    c: Coincident(g3,g4)
    c: Horizontal(g4)
    c: Coincident(g4,g5)
    c: Vertical(g5)
    c: Coincident(g5,g6)
    c: Vertical(g6)
    c: Coincident(g6,g7)
    c: Coincident(g7,g8)
    c: Horizontal(g8)
    c: Coincident(g8,g9)
    c: Coincident(g9,g0)
    c: Coincident(g10,g11)
    c: Horizontal(g11)
    c: Coincident(g11,g12)
    c: Coincident(g12,g13)
    c: Vertical(g13)
    c: Coincident(g13,g14)
    c: Horizontal(g14)
    c: Coincident(g14,g15)
    c: Vertical(g15)
    c: Coincident(g15,g10)
    c: Tangent(g16,g18) = -1.5708
    c: Tangent(g18,g17) = -1.5708
    c: Tangent(g17,g19) = -1.5708
    c: Tangent(g19,g16) = -1.5708
    c: Equal(g16,g17)
    c: Horizontal(g18)
    c: DistanceX(g18,g18) = 7
    c: Radius(g16) = 4
    c: DistanceY(g14,g-1) = 31.84
    c: DistanceX(g14,g-1) = 45.25
    c: DistanceY(g14,g17) = 3.5
    c: DistanceX(g14,g17) = 12
FEATURE [Sketcher::SketchObject] Sketch013
  ExternalGeometry = -> [Sketch]
  FullyConstrained = true
  Placement = pos=(0,0,4) rot=(0,0,1;0rad)
  sketch-geometry (20):
    g0: ArcOfCircle CenterX=-39.75 CenterY=25.5 CenterZ=0 NormalX=0 NormalY=0 NormalZ=1 AngleXU=0 Radius=7.5 StartAngle=1.5708 EndAngle=3.14159
    g1: LineSegment StartX=-39.75 StartY=33 StartZ=0 EndX=39.75 EndY=33 EndZ=0
    g2: ArcOfCircle CenterX=39.75 CenterY=25.5 CenterZ=0 NormalX=0 NormalY=0 NormalZ=1 AngleXU=0 Radius=7.5 StartAngle=1e-16 EndAngle=1.5708
    g3: LineSegment StartX=47.25 StartY=25.5 StartZ=0 EndX=47.25 EndY=-25.5 EndZ=0
    g4: ArcOfCircle CenterX=39.75 CenterY=-25.5 CenterZ=0 NormalX=0 NormalY=0 NormalZ=1 AngleXU=0 Radius=7.5 StartAngle=4.71239 EndAngle=6.28319
    g5: LineSegment StartX=39.75 StartY=-33 StartZ=0 EndX=-39.75 EndY=-33 EndZ=0
    g6: ArcOfCircle CenterX=-39.75 CenterY=-25.5 CenterZ=0 NormalX=0 NormalY=0 NormalZ=1 AngleXU=0 Radius=7.5 StartAngle=3.14159 EndAngle=4.71239
    g7: LineSegment StartX=-47.25 StartY=-25.5 StartZ=0 EndX=-47.25 EndY=25.5 EndZ=0
    g8: GeomPoint X=-47.25 Y=33 Z=0
    g9: GeomPoint X=47.25 Y=-33 Z=0
    g10: ArcOfCircle CenterX=-39.75 CenterY=25.5 CenterZ=0 NormalX=0 NormalY=0 NormalZ=1 AngleXU=0 Radius=5.3 StartAngle=1.5708 EndAngle=3.14159
    g11: LineSegment StartX=-39.75 StartY=30.8 StartZ=0 EndX=39.75 EndY=30.8 EndZ=0
    g12: ArcOfCircle CenterX=39.75 CenterY=25.5 CenterZ=0 NormalX=0 NormalY=0 NormalZ=1 AngleXU=0 Radius=5.3 StartAngle=1e-16 EndAngle=1.5708
    g13: LineSegment StartX=45.05 StartY=25.5 StartZ=0 EndX=45.05 EndY=-25.5 EndZ=0
    g14: ArcOfCircle CenterX=39.75 CenterY=-25.5 CenterZ=0 NormalX=0 NormalY=0 NormalZ=1 AngleXU=0 Radius=5.3 StartAngle=4.71239 EndAngle=6.28319
    g15: LineSegment StartX=39.75 StartY=-30.8 StartZ=0 EndX=-39.75 EndY=-30.8 EndZ=0
    g16: ArcOfCircle CenterX=-39.75 CenterY=-25.5 CenterZ=0 NormalX=0 NormalY=0 NormalZ=1 AngleXU=0 Radius=5.3 StartAngle=3.14159 EndAngle=4.71239
    g17: LineSegment StartX=-45.05 StartY=-25.5 StartZ=0 EndX=-45.05 EndY=25.5 EndZ=0
    g18: GeomPoint X=-45.05 Y=30.8 Z=0
    g19: GeomPoint X=45.05 Y=-30.8 Z=0
  constraints (45):
    c: Tangent(g0,g1) = 1.5708
    c: Tangent(g1,g2) = 1.5708
    c: Tangent(g2,g3) = 1.5708
    c: Tangent(g3,g4) = 1.5708
    c: Tangent(g4,g5) = 1.5708
    c: Tangent(g5,g6) = 1.5708
    c: Tangent(g6,g7) = 1.5708
    c: Tangent(g7,g0) = 1.5708
    c: Horizontal(g1)
    c: Horizontal(g5)
    c: Vertical(g3)
    c: Vertical(g7)
    c: Equal(g0,g2)
    c: Equal(g2,g4)
    c: Equal(g4,g6)
    c: PointOnObject(g8,g1)
    c: PointOnObject(g8,g7)
    c: PointOnObject(g9,g3)
    c: PointOnObject(g9,g5)
    c: Coincident(g0,g-3)
    c: Horizontal(g-3,g0)
    c: Tangent(g10,g11) = 1.5708
    c: Tangent(g12,g13) = 1.5708
    c: Tangent(g13,g14) = 1.5708
    c: Tangent(g14,g15) = 1.5708
    c: Tangent(g15,g16) = 1.5708
    c: Tangent(g16,g17) = 1.5708
    c: Tangent(g17,g10) = 1.5708
    c: Horizontal(g11)
    c: Horizontal(g15)
    c: Vertical(g13)
    c: Vertical(g17)
    c: Equal(g10,g12)
    c: Equal(g12,g14)
    c: Equal(g14,g16)
    c: PointOnObject(g18,g11)
    c: PointOnObject(g18,g17)
    c: PointOnObject(g19,g13)
    c: PointOnObject(g19,g15)
    c: Coincident(g14,g4)
    c: Coincident(g11,g12)
    c: Coincident(g0,g10)
    c: Vertical(g12,g11)
    c: Coincident(g14,g-4)
    c: DistanceX(g0,g10) = 2.2
FEATURE [Part::Extrusion] Extrude011  label="Extrude_inner"
  Base = -> Sketch013
  Dir = (0,0,1)
  DirMode = 2
  FaceMakerClass = Part::FaceMakerBullseye
  LengthFwd = 52
  LengthRev = 0
  Solid = true
  Symmetric = false
FEATURE [Sketcher::SketchObject] Sketch014
  ExternalGeometry = -> [Sketch013]
  FullyConstrained = true
  sketch-geometry (10):
    g0: ArcOfCircle CenterX=-39.75 CenterY=25.5 CenterZ=0 NormalX=0 NormalY=0 NormalZ=1 AngleXU=0 Radius=5.1 StartAngle=1.5708 EndAngle=3.14159
    g1: LineSegment StartX=-39.75 StartY=30.6 StartZ=0 EndX=39.75 EndY=30.6 EndZ=0
    g2: ArcOfCircle CenterX=39.75 CenterY=25.5 CenterZ=0 NormalX=0 NormalY=0 NormalZ=1 AngleXU=0 Radius=5.1 StartAngle=3e-16 EndAngle=1.5708
    g3: LineSegment StartX=44.85 StartY=25.5 StartZ=0 EndX=44.85 EndY=-25.5 EndZ=0
    g4: ArcOfCircle CenterX=39.75 CenterY=-25.5 CenterZ=0 NormalX=0 NormalY=0 NormalZ=1 AngleXU=0 Radius=5.1 StartAngle=4.71239 EndAngle=6.28319
    g5: LineSegment StartX=39.75 StartY=-30.6 StartZ=0 EndX=-39.75 EndY=-30.6 EndZ=0
    g6: ArcOfCircle CenterX=-39.75 CenterY=-25.5 CenterZ=0 NormalX=0 NormalY=0 NormalZ=1 AngleXU=0 Radius=5.1 StartAngle=3.14159 EndAngle=4.71239
    g7: LineSegment StartX=-44.85 StartY=-25.5 StartZ=0 EndX=-44.85 EndY=25.5 EndZ=0
    g8: GeomPoint X=-44.85 Y=30.6 Z=0
    g9: GeomPoint X=44.85 Y=-30.6 Z=0
  constraints (30):
    c: Horizontal(g1)
    c: Horizontal(g5)
    c: Vertical(g3)
    c: Vertical(g7)
    c: Equal(g0,g2)
    c: Equal(g2,g4)
    c: Equal(g4,g6)
    c: PointOnObject(g8,g1)
    c: PointOnObject(g8,g7)
    c: PointOnObject(g9,g3)
    c: PointOnObject(g9,g5)
    c: Coincident(g4,g-4)
    c: Coincident(g0,g-3)
    c: DistanceX(g-3,g0) = 0.2
    c: Coincident(g1,g0)
    c: Vertical(g0,g0)
    c: Coincident(g0,g7)
    c: Horizontal(g-3,g0)
    c: Coincident(g7,g6)
    c: Coincident(g5,g6)
    c: Horizontal(g6,g6)
    c: Vertical(g6,g5)
    c: Coincident(g3,g4)
    c: Coincident(g4,g5)
    c: Horizontal(g3,g-4)
    c: Vertical(g4,g-4)
    c: Coincident(g2,g3)
    c: Coincident(g1,g2)
    c: Vertical(g1,g2)
    c: Horizontal(g2,g2)
FEATURE [Part::Extrusion] Extrude012
  Base = -> Sketch014
  Dir = (0,0,1)
  DirMode = 2
  FaceMakerClass = Part::FaceMakerBullseye
  LengthFwd = 52
  LengthRev = 0
  Solid = true
  Symmetric = false
FEATURE [Part::Cut] Cut004
  Base = -> Extrude012
  Tool = -> Box001
FEATURE [Part::Box] Box008  label="Cube008"
  AttacherType = Attacher::AttachEngine3D
  Height = 100
  Length = 100
  Placement = pos=(-50,36.8,-0.6) rot=(1,0,0;0.523599rad)
  Width = 100
FEATURE [Part::Cut] Cut005
  Base = -> Cut004
  Tool = -> Box008
FEATURE [Part::FeaturePython] Facebinder  label="inner_bottom"  # WARN: FeaturePython — macro-defined, semantics opaque (R4)
  Area = 4267.09
  Extrusion = 0
  Faces = -> [Cut005]
  RemoveSplitter = false
  Sew = false
FEATURE [Part::FeaturePython] Facebinder001  label="inner_back"  # WARN: FeaturePython — macro-defined, semantics opaque (R4)
  Area = 3849.5
  Extrusion = 0
  Faces = -> [Cut005]
  RemoveSplitter = false
  Sew = false
FEATURE [Part::Extrusion] Extrude013
  Base = -> Facebinder
  Dir = (0,0.866025,0.5)
  DirMode = 2
  FaceMakerClass = Part::FaceMakerBullseye
  LengthFwd = 2
  LengthRev = 0
  Reversed = true
  Solid = false
  Symmetric = false
FEATURE [Part::Extrusion] Extrude014
  Base = -> Facebinder001
  Dir = (0,-0.5,0.866025)
  DirMode = 2
  FaceMakerClass = Part::FaceMakerBullseye
  LengthFwd = 1
  LengthRev = 0
  Reversed = true
  Solid = false
  Symmetric = false
FEATURE [Part::FeaturePython] Facebinder002  # WARN: FeaturePython — macro-defined, semantics opaque (R4)
  Area = 569.521
  Extrusion = 0
  Faces = -> [Connect]
  RemoveSplitter = false
  Sew = false
FEATURE [Sketcher::SketchObject] Sketch015
  FullyConstrained = false
  Placement = pos=(0,-20.65,35.7668) rot=(1,0,0;0.523599rad)
  sketch-geometry (16):
    g0: LineSegment StartX=-47.25 StartY=-5.6003 StartZ=0 EndX=-47.25 EndY=31.841 EndZ=0
    g1: ArcOfEllipse CenterX=-39.75 CenterY=-5.6003 CenterZ=0 NormalX=0 NormalY=-3e-16 NormalZ=1 MajorRadius=8.66025 MinorRadius=7.5 AngleXU=-3.14159 StartAngle=4.71239 EndAngle=6.28319
    g2: LineSegment StartX=39.75 StartY=-14.2606 StartZ=0 EndX=-39.75 EndY=-14.2606 EndZ=0
    g3: ArcOfEllipse CenterX=39.75 CenterY=-5.6003 CenterZ=0 NormalX=0 NormalY=-3e-16 NormalZ=1 MajorRadius=8.66025 MinorRadius=7.5 AngleXU=-3.14159 StartAngle=0 EndAngle=1.5708
    g4: LineSegment StartX=47.25 StartY=31.841 StartZ=0 EndX=47.25 EndY=-5.6003 EndZ=0
    g5: LineSegment StartX=47.25 StartY=33.841 StartZ=0 EndX=47.25 EndY=31.841 EndZ=0
    g6: LineSegment StartX=45.25 StartY=33.841 StartZ=0 EndX=47.25 EndY=33.841 EndZ=0
    g7: LineSegment StartX=-45.25 StartY=33.841 StartZ=0 EndX=45.25 EndY=33.841 EndZ=0
    g8: LineSegment StartX=-47.25 StartY=33.841 StartZ=0 EndX=-45.25 EndY=33.841 EndZ=0
    g9: LineSegment StartX=-47.25 StartY=31.841 StartZ=0 EndX=-47.25 EndY=33.841 EndZ=0
    g10: ArcOfEllipse CenterX=-39.75 CenterY=-5.6003 CenterZ=0 NormalX=0 NormalY=-3e-16 NormalZ=1 MajorRadius=6.35085 MinorRadius=5.5 AngleXU=-3.14159 StartAngle=4.71239 EndAngle=6.28319
    g11: LineSegment StartX=-45.25 StartY=-5.6003 StartZ=0 EndX=-45.25 EndY=31.841 EndZ=0
    g12: LineSegment StartX=-45.25 StartY=31.841 StartZ=0 EndX=45.25 EndY=31.841 EndZ=0
    g13: LineSegment StartX=45.25 StartY=31.841 StartZ=0 EndX=45.25 EndY=-5.6003 EndZ=0
    g14: ArcOfEllipse CenterX=39.75 CenterY=-5.6003 CenterZ=0 NormalX=0 NormalY=-3e-16 NormalZ=1 MajorRadius=6.35085 MinorRadius=5.5 AngleXU=-3.14159 StartAngle=0 EndAngle=1.5708
    g15: LineSegment StartX=39.75 StartY=-11.9512 StartZ=0 EndX=-39.75 EndY=-11.9512 EndZ=0
  constraints (28):
    c: Vertical(g0)
    c: Coincident(g0,g1)
    c: Coincident(g1,g2)
    c: Horizontal(g2)
    c: Coincident(g2,g3)
    c: Coincident(g3,g4)
    c: Vertical(g4)
    c: Coincident(g4,g5)
    c: Vertical(g5)
    c: Coincident(g5,g6)
    c: Horizontal(g6)
    c: Coincident(g6,g7)
    c: Horizontal(g7)
    c: Coincident(g7,g8)
    c: Horizontal(g8)
    c: Coincident(g8,g9)
    c: Vertical(g9)
    c: Coincident(g9,g0)
    c: Coincident(g10,g11)
    c: Vertical(g11)
    c: Coincident(g11,g12)
    c: Horizontal(g12)
    c: Coincident(g12,g13)
    c: Vertical(g13)
    c: Coincident(g13,g14)
    c: Coincident(g14,g15)
    c: Horizontal(g15)
    c: Coincident(g15,g10)
FEATURE [Part::Extrusion] Extrude015
  Base = -> Sketch015
  Dir = (0,-0.5,0.866025)
  DirMode = 2
  FaceMakerClass = Part::FaceMakerBullseye
  LengthFwd = 1
  LengthRev = 0
  Solid = true
  Symmetric = false
FEATURE [Part::FeaturePython] Connect003  label="inner_complete"  # WARN: FeaturePython — macro-defined, semantics opaque (R4)
  Objects = -> [Extrude013,Extrude014,Extrude015]
  Tolerance = 0
FEATURE [Sketcher::SketchObject] Sketch016
  ExternalGeometry = -> [Connect003]
  FullyConstrained = true
  Placement = pos=(0,0,0) rot=(0.57735,0.57735,0.57735;2.0944rad)
  sketch-geometry (3):
    g0: LineSegment StartX=5.45814 StartY=49.6857 StartZ=0 EndX=-16.1925 EndY=37.1857 EndZ=0
    g1: LineSegment StartX=5.45814 StartY=49.6857 StartZ=0 EndX=17.9581 EndY=28.0351 EndZ=0
    g2: ArcOfCircle CenterX=5.45814 CenterY=49.6857 CenterZ=0 NormalX=0 NormalY=0 NormalZ=1 AngleXU=0 Radius=25 StartAngle=3.66519 EndAngle=5.23599
  constraints (8):
    c: Coincident(g0,g-4)
    c: PointOnObject(g0,g-4)
    c: Coincident(g1,g0)
    c: PointOnObject(g1,g-3)
    c: Coincident(g2,g0)
    c: Coincident(g2,g0)
    c: Coincident(g2,g1)
    c: Distance(g0) = 25
FEATURE [Part::Extrusion] Extrude016
  Base = -> Sketch016
  Dir = (1,0,0)
  DirMode = 2
  FaceMakerClass = Part::FaceMakerBullseye
  LengthFwd = 1.2
  LengthRev = 0
  Placement = pos=(43.6,0,0) rot=(0,0,1;0rad)
  Solid = true
  Symmetric = false
FEATURE [Part::Extrusion] Extrude017
  Base = -> Sketch016
  Dir = (1,0,0)
  DirMode = 2
  FaceMakerClass = Part::FaceMakerBullseye
  LengthFwd = 1.2
  LengthRev = 0
  Placement = pos=(-44.7,0,0) rot=(0,0,1;0rad)
  Solid = true
  Symmetric = false
FEATURE [Sketcher::SketchObject] Sketch017
  ExternalGeometry = -> [Connect003,Extrude017,Extrude016]
  FullyConstrained = true
  MapMode = 5
  Placement = pos=(0,25.6081,14.7849) rot=(1,0,0;2.0944rad)
  Support = -> [Connect003]
  sketch-geometry (16):
    g0: LineSegment StartX=-43.5 StartY=40.3 StartZ=0 EndX=43.6 EndY=40.3 EndZ=0
    g1: LineSegment StartX=43.6 StartY=40.3 StartZ=0 EndX=43.6 EndY=20.3 EndZ=0
    g2: LineSegment StartX=-43.5 StartY=20.3 StartZ=0 EndX=-43.5 EndY=40.3 EndZ=0
    g3: LineSegment StartX=-40 StartY=20.3 StartZ=0 EndX=-43.5 EndY=20.3 EndZ=0
    g4: LineSegment StartX=-40 StartY=37.8 StartZ=0 EndX=-40 EndY=20.3 EndZ=0
    g5: LineSegment StartX=-29 StartY=37.8 StartZ=0 EndX=-40 EndY=37.8 EndZ=0
    g6: LineSegment StartX=-29 StartY=20.3 StartZ=0 EndX=-29 EndY=37.8 EndZ=0
    g7: LineSegment StartX=-20.5 StartY=20.3 StartZ=0 EndX=-29 EndY=20.3 EndZ=0
    g8: LineSegment StartX=-20.5 StartY=37.8 StartZ=0 EndX=-20.5 EndY=20.3 EndZ=0
    g9: LineSegment StartX=43.6 StartY=20.3 StartZ=0 EndX=23.5 EndY=20.3 EndZ=0
    g10: LineSegment StartX=23.5 StartY=20.3 StartZ=0 EndX=23.5 EndY=40.2 EndZ=0
    g11: LineSegment StartX=4 StartY=37.8 StartZ=0 EndX=-20.5 EndY=37.8 EndZ=0
    g12: LineSegment StartX=4 StartY=20.3 StartZ=0 EndX=4 EndY=37.8 EndZ=0
    g13: LineSegment StartX=11.5 StartY=20.3 StartZ=0 EndX=4 EndY=20.3 EndZ=0
    g14: LineSegment StartX=23.5 StartY=40.2 StartZ=0 EndX=11.5 EndY=40.2 EndZ=0
    g15: LineSegment StartX=11.5 StartY=40.2 StartZ=0 EndX=11.5 EndY=20.3 EndZ=0
  constraints (48):
    c: Coincident(g0,g1)
    c: Coincident(g1,g9)
    c: Coincident(g2,g0)
    c: Vertical(g1)
    c: Vertical(g2)
    c: PointOnObject(g0,g-3)
    c: PointOnObject(g0,g-5)
    c: PointOnObject(g0,g-4)
    c: Coincident(g4,g3)
    c: Coincident(g5,g4)
    c: Horizontal(g3)
    c: Vertical(g4)
    c: Coincident(g6,g5)
    c: Horizontal(g5)
    c: Coincident(g7,g6)
    c: Horizontal(g7)
    c: Coincident(g11,g8)
    c: Vertical(g6)
    c: Vertical(g8)
    c: DistanceX(g3,g3) = 3.5
    c: DistanceY(g4,g0) = 2.5
    c: Horizontal(g5,g11)
    c: Horizontal(g3,g6)
    c: Coincident(g8,g7)
    c: DistanceX(g7,g7) = 8.5
    c: DistanceX(g5,g5) = 11
    c: Coincident(g3,g2)
    c: DistanceY(g2,g2) = 20
    c: Coincident(g10,g14)
    c: Coincident(g9,g10)
    c: Horizontal(g9)
    c: Vertical(g10)
    c: Horizontal(g7,g9)
    c: Coincident(g12,g11)
    c: Horizontal(g11)
    c: Coincident(g13,g12)
    c: Coincident(g15,g13)
    c: Horizontal(g13)
    c: Coincident(g14,g15)
    c: Vertical(g15)
    c: Vertical(g12)
    c: DistanceX(g13,g13) = 7.5
    c: Horizontal(g7,g12)
    c: PointOnObject(g0,g-3)
    c: DistanceX(g11,g11) = 24.5
    c: DistanceX(g14,g14) = 12
    c: Horizontal(g14)
    c: DistanceY(g10,g-3) = 0.1
FEATURE [Part::Extrusion] Extrude018
  Base = -> Sketch017
  Dir = (0,-0.866025,-0.5)
  DirMode = 2
  FaceMakerClass = Part::FaceMakerBullseye
  LengthFwd = 2.5
  LengthRev = 0
  Solid = true
  Symmetric = false
FEATURE [Sketcher::SketchObject] Sketch018
  AttachmentOffset = pos=(0,0,2.5) rot=(0,0,1;0rad)
  ExternalGeometry = -> [Sketch017]
  FullyConstrained = true
  MapMode = 2
  Placement = pos=(0,23.4431,13.5349) rot=(1,0,0;2.0944rad)
  Support = -> [Sketch017]
  sketch-geometry (13):
    g0: LineSegment StartX=43.6 StartY=40.3 StartZ=0 EndX=43.6 EndY=20.3 EndZ=0
    g1: LineSegment StartX=26 StartY=20.3 StartZ=0 EndX=26 EndY=40.3 EndZ=0
    g2: LineSegment StartX=26 StartY=40.3 StartZ=0 EndX=43.6 EndY=40.3 EndZ=0
    g3: LineSegment StartX=-25.5 StartY=40.3 StartZ=0 EndX=-23 EndY=40.3 EndZ=0
    g4: LineSegment StartX=-25.5 StartY=40.3 StartZ=0 EndX=-25.5 EndY=20.3 EndZ=0
    g5: LineSegment StartX=-23 StartY=40.3 StartZ=0 EndX=-23 EndY=20.3 EndZ=0
    g6: LineSegment StartX=-25.5 StartY=20.3 StartZ=0 EndX=-23 EndY=20.3 EndZ=0
    g7: LineSegment StartX=-25.5 StartY=20.3 StartZ=0 EndX=-23 EndY=20.3 EndZ=0
    g8: LineSegment StartX=9 StartY=20.3 StartZ=0 EndX=6.5 EndY=20.3 EndZ=0
    g9: LineSegment StartX=6.5 StartY=20.3 StartZ=0 EndX=6.5 EndY=40.3 EndZ=0
    g10: LineSegment StartX=6.5 StartY=40.3 StartZ=0 EndX=9 EndY=40.3 EndZ=0
    g11: LineSegment StartX=9 StartY=40.3 StartZ=0 EndX=9 EndY=20.3 EndZ=0
    g12: LineSegment StartX=43.6 StartY=20.3 StartZ=0 EndX=26 EndY=20.3 EndZ=0
  constraints (36):
    c: Coincident(g0,g-5)
    c: Vertical(g1)
    c: Coincident(g2,g1)
    c: Coincident(g2,g0)
    c: PointOnObject(g3,g-3)
    c: PointOnObject(g3,g-3)
    c: Coincident(g4,g3)
    c: PointOnObject(g4,g-4)
    c: Vertical(g4)
    c: Coincident(g5,g3)
    c: PointOnObject(g5,g-4)
    c: Vertical(g5)
    c: Coincident(g6,g4)
    c: Coincident(g6,g5)
    c: Coincident(g7,g4)
    c: Coincident(g7,g5)
    c: Coincident(g8,g9)
    c: Coincident(g9,g10)
    c: Coincident(g10,g11)
    c: Horizontal(g10)
    c: Vertical(g9)
    c: PointOnObject(g9,g-3)
    c: Equal(g7,g8)
    c: DistanceX(g5,g-4) = 2.5
    c: Coincident(g8,g11)
    c: Vertical(g11)
    c: DistanceX(g7,g7) = 2.5
    c: Horizontal(g8)
    c: Horizontal(g8,g-6)
    c: DistanceX(g-6,g8) = 2.5
    c: Coincident(g12,g0)
    c: Coincident(g12,g1)
    c: DistanceX(g-5,g1) = 2.5
    c: PointOnObject(g1,g-5)
    c: PointOnObject(g1,g-3)
    c: Coincident(g0,g-3)
FEATURE [Part::Extrusion] Extrude019
  Base = -> Sketch018
  Dir = (0,-0.866025,-0.5)
  DirMode = 2
  FaceMakerClass = Part::FaceMakerBullseye
  LengthFwd = 2
  LengthRev = 0
  Solid = true
  Symmetric = false
FEATURE [Sketcher::SketchObject] Sketch019
  AttachmentOffset = pos=(0,0,4.5) rot=(0,0,1;0rad)
  ExternalGeometry = -> [Sketch017]
  FullyConstrained = true
  MapMode = 2
  Placement = pos=(0,21.711,12.5349) rot=(1,0,0;2.0944rad)
  Support = -> [Sketch017]
  sketch-geometry (18):
    g0: LineSegment StartX=-43.5 StartY=40.3 StartZ=0 EndX=-40 EndY=40.3 EndZ=0
    g1: LineSegment StartX=-40 StartY=40.3 StartZ=0 EndX=-40 EndY=20.3 EndZ=0
    g2: LineSegment StartX=-40 StartY=20.3 StartZ=0 EndX=-43.5 EndY=20.3 EndZ=0
    g3: LineSegment StartX=-43.5 StartY=20.3 StartZ=0 EndX=-43.5 EndY=40.3 EndZ=0
    g4: LineSegment StartX=-29 StartY=40.3 StartZ=0 EndX=-20.5 EndY=40.3 EndZ=0
    g5: LineSegment StartX=-20.5 StartY=40.3 StartZ=0 EndX=-20.5 EndY=20.3 EndZ=0
    g6: LineSegment StartX=-20.5 StartY=20.3 StartZ=0 EndX=-25.5 EndY=20.3 EndZ=0
    g7: LineSegment StartX=4 StartY=40.3 StartZ=0 EndX=11.5 EndY=40.3 EndZ=0
    g8: LineSegment StartX=11.5 StartY=40.3 StartZ=0 EndX=11.5 EndY=20.3 EndZ=0
    g9: LineSegment StartX=11.5 StartY=20.3 StartZ=0 EndX=4 EndY=20.3 EndZ=0
    g10: LineSegment StartX=4 StartY=20.3 StartZ=0 EndX=4 EndY=40.3 EndZ=0
    g11: LineSegment StartX=23.5 StartY=40.3 StartZ=0 EndX=43.6 EndY=40.3 EndZ=0
    g12: LineSegment StartX=43.6 StartY=40.3 StartZ=0 EndX=43.6 EndY=20.3 EndZ=0
    g13: LineSegment StartX=43.6 StartY=20.3 StartZ=0 EndX=23.5 EndY=20.3 EndZ=0
    g14: LineSegment StartX=23.5 StartY=20.3 StartZ=0 EndX=23.5 EndY=40.3 EndZ=0
    g15: LineSegment StartX=-29 StartY=35.3 StartZ=0 EndX=-29 EndY=40.3 EndZ=0
    g16: LineSegment StartX=-25.5 StartY=20.3 StartZ=0 EndX=-25.5 EndY=35.3 EndZ=0
    g17: LineSegment StartX=-25.5 StartY=35.3 StartZ=0 EndX=-29 EndY=35.3 EndZ=0
  constraints (47):
    c: Coincident(g0,g1)
    c: Coincident(g1,g2)
    c: Coincident(g2,g3)
    c: Coincident(g3,g0)
    c: Horizontal(g0)
    c: Horizontal(g2)
    c: Vertical(g1)
    c: Vertical(g3)
    c: Coincident(g0,g-3)
    c: Coincident(g1,g-4)
    c: Coincident(g4,g5)
    c: Coincident(g5,g6)
    c: Coincident(g15,g4)
    c: Horizontal(g4)
    c: Vertical(g5)
    c: Horizontal(g4,g0)
    c: Coincident(g-5,g5)
    c: Coincident(g7,g8)
    c: Coincident(g8,g9)
    c: Coincident(g9,g10)
    c: Coincident(g10,g7)
    c: Horizontal(g7)
    c: Vertical(g8)
    c: Vertical(g10)
    c: Horizontal(g0,g7)
    c: Coincident(g9,g-6)
    c: Coincident(g8,g-6)
    c: Coincident(g11,g12)
    c: Coincident(g12,g13)
    c: Coincident(g13,g14)
    c: Coincident(g14,g11)
    c: Horizontal(g11)
    c: Vertical(g12)
    c: Vertical(g14)
    c: Coincident(g13,g-7)
    c: Coincident(g12,g-7)
    c: Horizontal(g0,g11)
    c: Coincident(g17,g15)
    c: Vertical(g15)
    c: Coincident(g16,g17)
    c: Vertical(g16)
    c: Coincident(g6,g16)
    c: PointOnObject(g6,g-5)
    c: DistanceX(g6,g6) = 5
    c: Horizontal(g17)
    c: DistanceY(g15,g15) = 5
    c: Vertical(g-5,g15)
FEATURE [Part::Extrusion] Extrude020
  Base = -> Sketch019
  Dir = (0,-0.866025,-0.5)
  DirMode = 2
  FaceMakerClass = Part::FaceMakerBullseye
  LengthFwd = 2
  LengthRev = 0
  Solid = true
  Symmetric = false
FEATURE [Part::FeaturePython] Connect004  # WARN: FeaturePython — macro-defined, semantics opaque (R4)
  Objects = -> [Extrude020,Extrude019,Extrude018,Extrude017,Extrude016,Connect003]
  Tolerance = 0
FEATURE [Sketcher::SketchObject] Sketch020
  ExternalGeometry = -> [Extrude020,Extrude018]
  FullyConstrained = false
  MapMode = 5
  Placement = pos=(0,-21.15,36.6329) rot=(1,0,0;0.523599rad)
  Support = -> [Connect004]
  sketch-geometry (27):
    g0: ArcOfCircle CenterX=-17.5 CenterY=24.7697 CenterZ=0 NormalX=0 NormalY=0 NormalZ=1 AngleXU=0 Radius=2 StartAngle=1.5708 EndAngle=4.71239
    g1: ArcOfCircle CenterX=1 CenterY=24.7697 CenterZ=0 NormalX=0 NormalY=0 NormalZ=1 AngleXU=0 Radius=2 StartAngle=4.71239 EndAngle=7.85398
    g2: LineSegment StartX=-17.5 StartY=22.7697 StartZ=0 EndX=1 EndY=22.7697 EndZ=0
    g3: LineSegment StartX=1 StartY=26.7697 StartZ=0 EndX=-17.5 EndY=26.7697 EndZ=0
    g4: ArcOfCircle CenterX=-31.5 CenterY=24.7697 CenterZ=0 NormalX=0 NormalY=0 NormalZ=1 AngleXU=0 Radius=2 StartAngle=4.71239 EndAngle=7.85398
    g5: ArcOfCircle CenterX=-37.5 CenterY=24.7697 CenterZ=0 NormalX=0 NormalY=0 NormalZ=1 AngleXU=0 Radius=2 StartAngle=1.5708 EndAngle=4.71239
    g6: LineSegment StartX=-31.5 StartY=26.7697 StartZ=0 EndX=-37.5 EndY=26.7697 EndZ=0
    g7: LineSegment StartX=-37.5 StartY=22.7697 StartZ=0 EndX=-31.5 EndY=22.7697 EndZ=0
    g8: ArcOfCircle CenterX=14.5 CenterY=24.7697 CenterZ=0 NormalX=0 NormalY=0 NormalZ=1 AngleXU=0 Radius=2 StartAngle=1.5708 EndAngle=4.71239
    g9: ArcOfCircle CenterX=20.5 CenterY=24.7697 CenterZ=0 NormalX=0 NormalY=0 NormalZ=1 AngleXU=0 Radius=2 StartAngle=4.71239 EndAngle=7.85398
    g10: LineSegment StartX=14.5 StartY=22.7697 StartZ=0 EndX=20.5 EndY=22.7697 EndZ=0
    g11: LineSegment StartX=20.5 StartY=26.7697 StartZ=0 EndX=14.5 EndY=26.7697 EndZ=0
    g12: LineSegment StartX=28.5 StartY=29.5697 StartZ=0 EndX=33.5 EndY=29.5697 EndZ=0
    g13: LineSegment StartX=33.5 StartY=29.5697 StartZ=0 EndX=33.5 EndY=24.5697 EndZ=0
    g14: LineSegment StartX=33.5 StartY=24.5697 StartZ=0 EndX=28.5 EndY=24.5697 EndZ=0
    g15: LineSegment StartX=28.5 StartY=24.5697 StartZ=0 EndX=28.5 EndY=29.5697 EndZ=0
    g16: LineSegment StartX=36 StartY=29.5697 StartZ=0 EndX=41 EndY=29.5697 EndZ=0
    g17: LineSegment StartX=41 StartY=29.5697 StartZ=0 EndX=41 EndY=24.5697 EndZ=0
    g18: LineSegment StartX=41 StartY=24.5697 StartZ=0 EndX=36 EndY=24.5697 EndZ=0
    g19: LineSegment StartX=36 StartY=24.5697 StartZ=0 EndX=36 EndY=29.5697 EndZ=0
    g20: GeomPoint X=26.6822 Y=52.4741 Z=0
    g21: LineSegment StartX=-40 StartY=25.0697 StartZ=0 EndX=-37.5 EndY=24.7697 EndZ=0
    g22: LineSegment StartX=-31.5 StartY=24.7697 StartZ=0 EndX=-29 EndY=25.0697 EndZ=0
    g23: LineSegment StartX=1 StartY=24.7697 StartZ=0 EndX=4 EndY=25.0697 EndZ=0
    g24: LineSegment StartX=-20.5 StartY=25.0697 StartZ=0 EndX=-17.5 EndY=24.7697 EndZ=0
    g25: LineSegment StartX=11.5 StartY=25.0697 StartZ=0 EndX=14.5 EndY=24.7697 EndZ=0
    g26: LineSegment StartX=20.5 StartY=24.7697 StartZ=0 EndX=23.5 EndY=25.0697 EndZ=0
  constraints (66):
    c: Tangent(g0,g2) = -1.5708
    c: Tangent(g2,g1) = -1.5708
    c: Tangent(g1,g3) = -1.5708
    c: Tangent(g3,g0) = -1.5708
    c: Equal(g0,g1)
    c: Horizontal(g2)
    c: DistanceY(g1,g1) = 4
    c: DistanceX(g3,g3) = 18.5
    c: Tangent(g4,g6) = -1.5708
    c: Tangent(g6,g5) = -1.5708
    c: Tangent(g5,g7) = -1.5708
    c: Tangent(g7,g4) = -1.5708
    c: Equal(g4,g5)
    c: Horizontal(g6)
    c: Equal(g4,g1)
    c: Tangent(g8,g10) = -1.5708
    c: Tangent(g10,g9) = -1.5708
    c: Tangent(g9,g11) = -1.5708
    c: Tangent(g11,g8) = -1.5708
    c: Equal(g8,g9)
    c: Equal(g5,g8)
    c: Coincident(g12,g13)
    c: Coincident(g13,g14)
    c: Coincident(g14,g15)
    c: Coincident(g15,g12)
    c: Horizontal(g12)
    c: Horizontal(g14)
    c: Vertical(g13)
    c: Vertical(g15)
    c: Coincident(g16,g17)
    c: Coincident(g17,g18)
    c: Coincident(g18,g19)
    c: Coincident(g19,g16)
    c: Horizontal(g16)
    c: Horizontal(g18)
    c: Vertical(g17)
    c: Vertical(g19)
    c: PointOnObject(g12,g-5)
    c: PointOnObject(g16,g-5)
    c: Equal(g18,g14)
    c: DistanceX(g13,g18) = 2.5
    c: DistanceX(g14,g14) = 5
    c: DistanceY(g15,g15) = 5
    c: Horizontal(g13,g18)
    c: DistanceX(g-4,g14) = 5
    c: DistanceX(g6,g6) = 6
    c: DistanceY(g5,g-6) = 0.3
    c: Coincident(g21,g-7)
    c: Coincident(g21,g5)
    c: Coincident(g22,g4)
    c: Coincident(g22,g-8)
    c: Equal(g21,g22)
    c: Coincident(g23,g1)
    c: Coincident(g23,g-10)
    c: Coincident(g24,g-9)
    c: Coincident(g24,g0)
    c: Equal(g24,g23)
    c: Horizontal(g4,g0)
    c: Horizontal(g11)
    c: Coincident(g25,g-11)
    c: Coincident(g25,g8)
    c: Coincident(g26,g9)
    c: Coincident(g26,g-4)
    c: Equal(g25,g26)
    c: Horizontal(g1,g8)
    c: DistanceX(g11,g11) = 6
FEATURE [Part::Extrusion] Extrude021
  Base = -> Sketch020
  Dir = (0,-0.5,0.866025)
  DirMode = 2
  FaceMakerClass = Part::FaceMakerBullseye
  LengthFwd = 25
  LengthRev = 0
  Reversed = true
  Solid = true
  Symmetric = false
FEATURE [Part::Cut] Cut006  label="Inner_complete"
  Base = -> Connect004
  Tool = -> Extrude021
